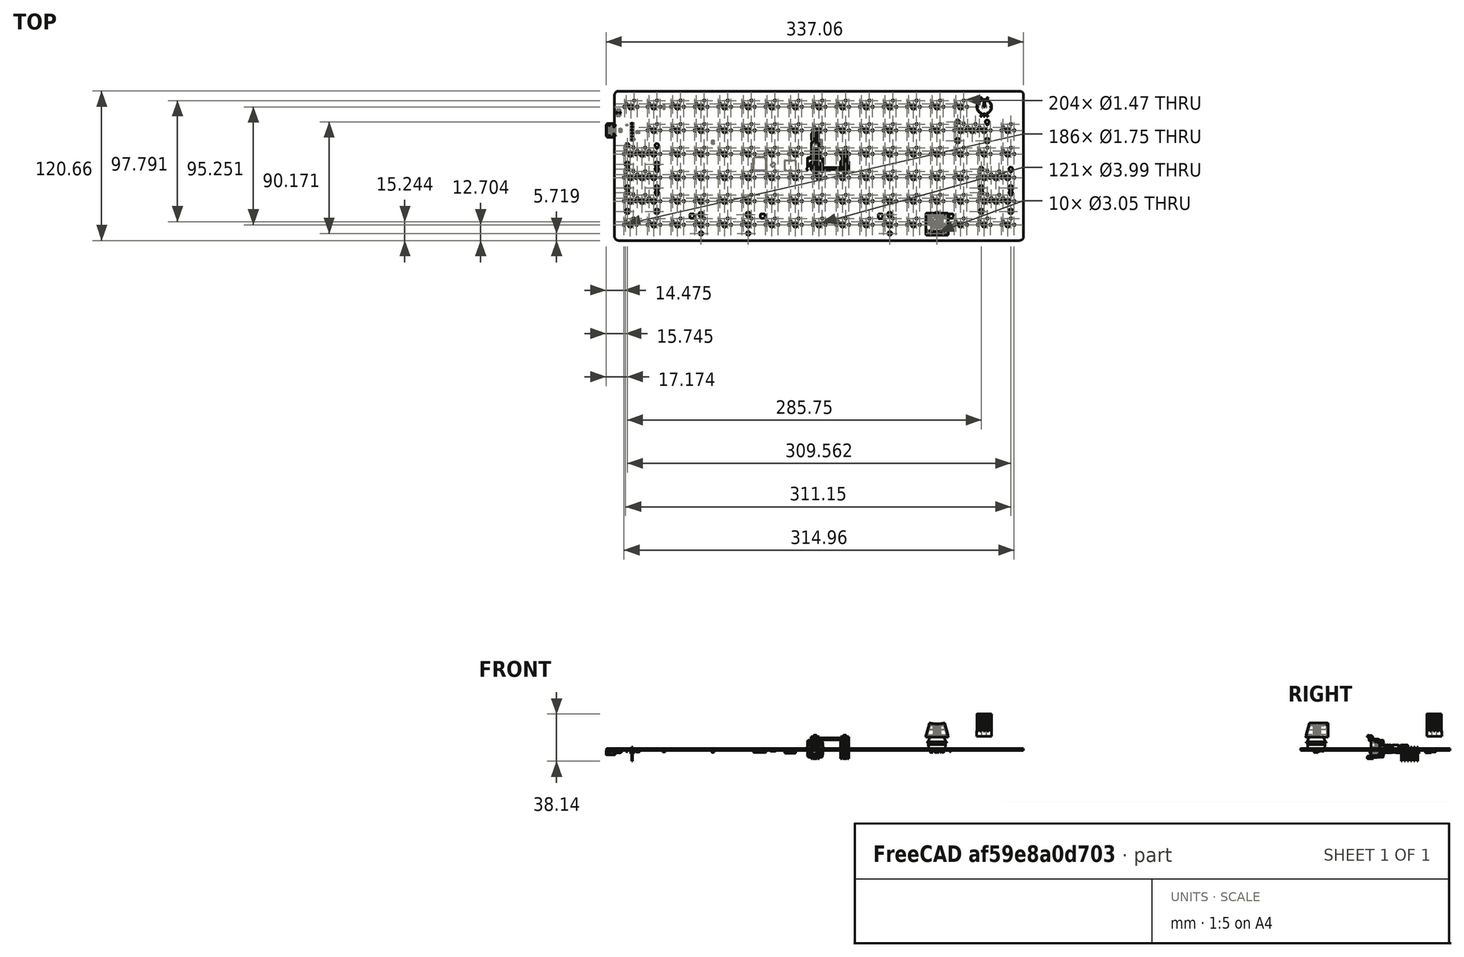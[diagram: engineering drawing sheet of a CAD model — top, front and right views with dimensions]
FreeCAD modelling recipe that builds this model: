
FCSTD DOCUMENT  (FreeCAD 0.19R24291 (Git))
Label: Orthonite87_003
License: All rights reserved
LicenseURL: http://en.wikipedia.org/wiki/All_rights_reserved
objects: App::Link×376, Part::Feature×31, App::Part×8, PartDesign::CoordinateSystem×1, Sketcher::SketchObject×1
note: 33 computed .brp shape members not serialized (recipe doc carries the construction recipe); baked Part::Feature solids carry a one-line shape summary decoded from their .brp

FEATURE [PartDesign::CoordinateSystem] Local_CS_e1db
  AttacherType = Attacher::AttachEngine3D
FEATURE [Part::Feature] Pcb_e1db
  Placement = pos=(-174.625,80.9625,0) rot=(0,0,1;0rad)
  shape: bbox 336.6 x 120.7 x 1.6 mm, 675 faces (baked)
FEATURE [Sketcher::SketchObject] PCB_Sketch_e1db
  FullyConstrained = false
  sketch-geometry (18):
    g0: LineSegment StartX=-168.275 StartY=33.3375 StartZ=0 EndX=-168.275 EndY=23.8125 EndZ=0
    g1: LineSegment StartX=-163.512 StartY=23.0188 StartZ=0 EndX=-162.719 EndY=23.0188 EndZ=0
    g2: LineSegment StartX=-163.512 StartY=34.1313 StartZ=0 EndX=-162.719 EndY=34.1313 EndZ=0
    g3: LineSegment StartX=-167.481 StartY=34.1313 StartZ=0 EndX=-163.512 EndY=34.1313 EndZ=0
    g4: LineSegment StartX=-163.512 StartY=23.0188 StartZ=0 EndX=-167.481 EndY=23.0188 EndZ=0
    g5: LineSegment StartX=-161.925 StartY=22.225 StartZ=0 EndX=-161.925 EndY=-57.15 EndZ=0
    g6: LineSegment StartX=-161.925 StartY=57.15 StartZ=0 EndX=-161.925 EndY=34.925 EndZ=0
    g7: LineSegment StartX=168.275 StartY=-57.15 StartZ=0 EndX=168.275 EndY=57.15 EndZ=0
    g8: LineSegment StartX=-158.75 StartY=-60.325 StartZ=0 EndX=165.1 EndY=-60.325 EndZ=0
    g9: LineSegment StartX=-158.75 StartY=60.325 StartZ=0 EndX=165.1 EndY=60.325 EndZ=0
    g10: ArcOfCircle CenterX=-167.481 CenterY=33.3375 CenterZ=0 NormalX=0 NormalY=0 NormalZ=1 AngleXU=0 Radius=0.79375 StartAngle=1.5708 EndAngle=3.14159
    g11: ArcOfCircle CenterX=-167.481 CenterY=23.8125 CenterZ=0 NormalX=0 NormalY=0 NormalZ=1 AngleXU=0 Radius=0.79375 StartAngle=3.14159 EndAngle=4.71239
    g12: ArcOfCircle CenterX=-162.719 CenterY=22.225 CenterZ=0 NormalX=0 NormalY=0 NormalZ=1 AngleXU=0 Radius=0.79375 StartAngle=0 EndAngle=1.5708
    g13: ArcOfCircle CenterX=-162.719 CenterY=34.925 CenterZ=0 NormalX=0 NormalY=0 NormalZ=1 AngleXU=0 Radius=0.79375 StartAngle=4.71239 EndAngle=6.28319
    g14: ArcOfCircle CenterX=165.1 CenterY=-57.15 CenterZ=0 NormalX=0 NormalY=0 NormalZ=1 AngleXU=0 Radius=3.175 StartAngle=4.71239 EndAngle=6.28319
    g15: ArcOfCircle CenterX=-158.75 CenterY=-57.15 CenterZ=0 NormalX=0 NormalY=0 NormalZ=1 AngleXU=0 Radius=3.175 StartAngle=3.14159 EndAngle=4.71239
    g16: ArcOfCircle CenterX=-158.75 CenterY=57.15 CenterZ=0 NormalX=0 NormalY=0 NormalZ=1 AngleXU=0 Radius=3.175 StartAngle=1.5708 EndAngle=3.14159
    g17: ArcOfCircle CenterX=165.1 CenterY=57.15 CenterZ=0 NormalX=0 NormalY=0 NormalZ=1 AngleXU=0 Radius=3.175 StartAngle=0 EndAngle=1.5708
FEATURE [Part::Feature] Shape  label="K_105_cherry mx_611CBFA4"
  Placement = pos=(98.425,-47.6255,5.5) rot=(0,0.707107,0.707107;3.14159rad)
  shape: bbox 15.64 x 16.33 x 17.85 mm, 92 faces (baked)
FEATURE [Part::Feature] Shape001  label="K_105_MX 轴标准键帽__¨¹_¡À__¡§1__¨¤_611CBFA4[2]"
  Placement = pos=(89.425,-38.1255,9.5) rot=(1,0,0;1.5708rad)
  shape: bbox 18.01 x 18 x 11.38 mm, 348 faces (baked)
FEATURE [App::Link] K_105_cherry_mx_611CBFA4_ln_  label="K_108_105_cherry mx_611DE0BA"
  LinkPlacement = pos=(155.575,-47.6255,5.5) rot=(0,0.707107,0.707107;3.14159rad)
  LinkedObject = -> Shape
  Placement = pos=(155.575,-47.6255,5.5) rot=(0,0.707107,0.707107;3.14159rad)
FEATURE [App::Link] K_105_MX______________________________________1_______611CBFA4_2__ln_  label="K_108_105_MX 轴标准键帽__¨¹_¡À__¡§1__¨¤_611DE0BA[2]"
  LinkPlacement = pos=(146.575,-38.1255,9.5) rot=(1,0,0;1.5708rad)
  LinkedObject = -> Shape001
  Placement = pos=(146.575,-38.1255,9.5) rot=(1,0,0;1.5708rad)
FEATURE [App::Link] K_105_cherry_mx_611CBFA4_ln_001  label="K_107_105_cherry mx_611DE0A5"
  LinkPlacement = pos=(136.525,-47.6255,5.5) rot=(0,0.707107,0.707107;3.14159rad)
  LinkedObject = -> Shape
  Placement = pos=(136.525,-47.6255,5.5) rot=(0,0.707107,0.707107;3.14159rad)
FEATURE [App::Link] K_105_MX______________________________________1_______611CBFA4_2__ln_001  label="K_107_105_MX 轴标准键帽__¨¹_¡À__¡§1__¨¤_611DE0A5[2]"
  LinkPlacement = pos=(127.525,-38.1255,9.5) rot=(1,0,0;1.5708rad)
  LinkedObject = -> Shape001
  Placement = pos=(127.525,-38.1255,9.5) rot=(1,0,0;1.5708rad)
FEATURE [App::Link] K_105_cherry_mx_611CBFA4_ln_002  label="K_106_105_cherry mx_611DE090"
  LinkPlacement = pos=(117.475,-47.6255,5.5) rot=(0,0.707107,0.707107;3.14159rad)
  LinkedObject = -> Shape
  Placement = pos=(117.475,-47.6255,5.5) rot=(0,0.707107,0.707107;3.14159rad)
FEATURE [App::Link] K_105_MX______________________________________1_______611CBFA4_2__ln_002  label="K_106_105_MX 轴标准键帽__¨¹_¡À__¡§1__¨¤_611DE090[2]"
  LinkPlacement = pos=(108.475,-38.1255,9.5) rot=(1,0,0;1.5708rad)
  LinkedObject = -> Shape001
  Placement = pos=(108.475,-38.1255,9.5) rot=(1,0,0;1.5708rad)
FEATURE [App::Link] K_105_cherry_mx_611CBFA4_ln_003  label="K_103_105_cherry mx_611DE023"
  LinkPlacement = pos=(60.325,-47.6255,5.5) rot=(0,0.707107,0.707107;3.14159rad)
  LinkedObject = -> Shape
  Placement = pos=(60.325,-47.6255,5.5) rot=(0,0.707107,0.707107;3.14159rad)
FEATURE [App::Link] K_105_MX______________________________________1_______611CBFA4_2__ln_003  label="K_103_105_MX 轴标准键帽__¨¹_¡À__¡§1__¨¤_611DE023[2]"
  LinkPlacement = pos=(51.325,-38.1255,9.5) rot=(1,0,0;1.5708rad)
  LinkedObject = -> Shape001
  Placement = pos=(51.325,-38.1255,9.5) rot=(1,0,0;1.5708rad)
FEATURE [App::Link] K_105_cherry_mx_611CBFA4_ln_004  label="K_102_105_cherry mx_611DE00E"
  LinkPlacement = pos=(41.275,-47.6255,5.5) rot=(0,0.707107,0.707107;3.14159rad)
  LinkedObject = -> Shape
  Placement = pos=(41.275,-47.6255,5.5) rot=(0,0.707107,0.707107;3.14159rad)
FEATURE [App::Link] K_105_MX______________________________________1_______611CBFA4_2__ln_004  label="K_102_105_MX 轴标准键帽__¨¹_¡À__¡§1__¨¤_611DE00E[2]"
  LinkPlacement = pos=(32.275,-38.1255,9.5) rot=(1,0,0;1.5708rad)
  LinkedObject = -> Shape001
  Placement = pos=(32.275,-38.1255,9.5) rot=(1,0,0;1.5708rad)
FEATURE [App::Link] K_105_cherry_mx_611CBFA4_ln_005  label="K_101_105_cherry mx_611DDFF9"
  LinkPlacement = pos=(22.225,-47.6255,5.5) rot=(0,0.707107,0.707107;3.14159rad)
  LinkedObject = -> Shape
  Placement = pos=(22.225,-47.6255,5.5) rot=(0,0.707107,0.707107;3.14159rad)
FEATURE [App::Link] K_105_MX______________________________________1_______611CBFA4_2__ln_005  label="K_101_105_MX 轴标准键帽__¨¹_¡À__¡§1__¨¤_611DDFF9[2]"
  LinkPlacement = pos=(13.225,-38.1255,9.5) rot=(1,0,0;1.5708rad)
  LinkedObject = -> Shape001
  Placement = pos=(13.225,-38.1255,9.5) rot=(1,0,0;1.5708rad)
FEATURE [App::Link] K_105_cherry_mx_611CBFA4_ln_006  label="K_100_105_cherry mx_611DDFE4"
  LinkPlacement = pos=(3.175,-47.6255,5.5) rot=(0,0.707107,0.707107;3.14159rad)
  LinkedObject = -> Shape
  Placement = pos=(3.175,-47.6255,5.5) rot=(0,0.707107,0.707107;3.14159rad)
FEATURE [App::Link] K_105_MX______________________________________1_______611CBFA4_2__ln_006  label="K_100_105_MX 轴标准键帽__¨¹_¡À__¡§1__¨¤_611DDFE4[2]"
  LinkPlacement = pos=(-5.825,-38.1255,9.5) rot=(1,0,0;1.5708rad)
  LinkedObject = -> Shape001
  Placement = pos=(-5.825,-38.1255,9.5) rot=(1,0,0;1.5708rad)
FEATURE [App::Link] K_105_cherry_mx_611CBFA4_ln_007  label="K_2_105_cherry mx_611DD732"
  LinkPlacement = pos=(-148.717,47.625,5.5) rot=(0,0.707107,0.707107;3.14159rad)
  LinkedObject = -> Shape
  Placement = pos=(-148.717,47.625,5.5) rot=(0,0.707107,0.707107;3.14159rad)
FEATURE [App::Link] K_105_MX______________________________________1_______611CBFA4_2__ln_007  label="K_2_105_MX 轴标准键帽__¨¹_¡À__¡§1__¨¤_611DD732[2]"
  LinkPlacement = pos=(-157.717,57.125,9.5) rot=(1,0,0;1.5708rad)
  LinkedObject = -> Shape001
  Placement = pos=(-157.717,57.125,9.5) rot=(1,0,0;1.5708rad)
FEATURE [App::Link] K_105_cherry_mx_611CBFA4_ln_008  label="K_9_105_cherry mx_611DD7C5"
  LinkPlacement = pos=(-15.875,47.625,5.5) rot=(0,0.707107,0.707107;3.14159rad)
  LinkedObject = -> Shape
  Placement = pos=(-15.875,47.625,5.5) rot=(0,0.707107,0.707107;3.14159rad)
FEATURE [App::Link] K_105_MX______________________________________1_______611CBFA4_2__ln_008  label="K_9_105_MX 轴标准键帽__¨¹_¡À__¡§1__¨¤_611DD7C5[2]"
  LinkPlacement = pos=(-24.875,57.125,9.5) rot=(1,0,0;1.5708rad)
  LinkedObject = -> Shape001
  Placement = pos=(-24.875,57.125,9.5) rot=(1,0,0;1.5708rad)
FEATURE [App::Link] K_105_cherry_mx_611CBFA4_ln_009  label="K_8_105_cherry mx_611DD7B0"
  LinkPlacement = pos=(-34.925,47.625,5.5) rot=(0,0.707107,0.707107;3.14159rad)
  LinkedObject = -> Shape
  Placement = pos=(-34.925,47.625,5.5) rot=(0,0.707107,0.707107;3.14159rad)
FEATURE [App::Link] K_105_MX______________________________________1_______611CBFA4_2__ln_009  label="K_8_105_MX 轴标准键帽__¨¹_¡À__¡§1__¨¤_611DD7B0[2]"
  LinkPlacement = pos=(-43.925,57.125,9.5) rot=(1,0,0;1.5708rad)
  LinkedObject = -> Shape001
  Placement = pos=(-43.925,57.125,9.5) rot=(1,0,0;1.5708rad)
FEATURE [App::Link] K_105_cherry_mx_611CBFA4_ln_010  label="K_7_105_cherry mx_611DD79B"
  LinkPlacement = pos=(-53.975,47.625,5.5) rot=(0,0.707107,0.707107;3.14159rad)
  LinkedObject = -> Shape
  Placement = pos=(-53.975,47.625,5.5) rot=(0,0.707107,0.707107;3.14159rad)
FEATURE [App::Link] K_105_MX______________________________________1_______611CBFA4_2__ln_010  label="K_7_105_MX 轴标准键帽__¨¹_¡À__¡§1__¨¤_611DD79B[2]"
  LinkPlacement = pos=(-62.975,57.125,9.5) rot=(1,0,0;1.5708rad)
  LinkedObject = -> Shape001
  Placement = pos=(-62.975,57.125,9.5) rot=(1,0,0;1.5708rad)
FEATURE [App::Link] K_105_cherry_mx_611CBFA4_ln_011  label="K_6_105_cherry mx_611DD786"
  LinkPlacement = pos=(-73.025,47.625,5.5) rot=(0,0.707107,0.707107;3.14159rad)
  LinkedObject = -> Shape
  Placement = pos=(-73.025,47.625,5.5) rot=(0,0.707107,0.707107;3.14159rad)
FEATURE [App::Link] K_105_MX______________________________________1_______611CBFA4_2__ln_011  label="K_6_105_MX 轴标准键帽__¨¹_¡À__¡§1__¨¤_611DD786[2]"
  LinkPlacement = pos=(-82.025,57.125,9.5) rot=(1,0,0;1.5708rad)
  LinkedObject = -> Shape001
  Placement = pos=(-82.025,57.125,9.5) rot=(1,0,0;1.5708rad)
FEATURE [App::Link] K_105_cherry_mx_611CBFA4_ln_012  label="K_5_105_cherry mx_611DD771"
  LinkPlacement = pos=(-92.075,47.625,5.5) rot=(0,0.707107,0.707107;3.14159rad)
  LinkedObject = -> Shape
  Placement = pos=(-92.075,47.625,5.5) rot=(0,0.707107,0.707107;3.14159rad)
FEATURE [App::Link] K_105_MX______________________________________1_______611CBFA4_2__ln_012  label="K_5_105_MX 轴标准键帽__¨¹_¡À__¡§1__¨¤_611DD771[2]"
  LinkPlacement = pos=(-101.075,57.125,9.5) rot=(1,0,0;1.5708rad)
  LinkedObject = -> Shape001
  Placement = pos=(-101.075,57.125,9.5) rot=(1,0,0;1.5708rad)
FEATURE [App::Link] K_105_cherry_mx_611CBFA4_ln_013  label="K_4_105_cherry mx_611DD75C"
  LinkPlacement = pos=(-111.125,47.625,5.5) rot=(0,0.707107,0.707107;3.14159rad)
  LinkedObject = -> Shape
  Placement = pos=(-111.125,47.625,5.5) rot=(0,0.707107,0.707107;3.14159rad)
FEATURE [App::Link] K_105_MX______________________________________1_______611CBFA4_2__ln_013  label="K_4_105_MX 轴标准键帽__¨¹_¡À__¡§1__¨¤_611DD75C[2]"
  LinkPlacement = pos=(-120.125,57.125,9.5) rot=(1,0,0;1.5708rad)
  LinkedObject = -> Shape001
  Placement = pos=(-120.125,57.125,9.5) rot=(1,0,0;1.5708rad)
FEATURE [App::Link] K_105_cherry_mx_611CBFA4_ln_014  label="K_3_105_cherry mx_611DD747"
  LinkPlacement = pos=(-130.175,47.625,5.5) rot=(0,0.707107,0.707107;3.14159rad)
  LinkedObject = -> Shape
  Placement = pos=(-130.175,47.625,5.5) rot=(0,0.707107,0.707107;3.14159rad)
FEATURE [App::Link] K_105_MX______________________________________1_______611CBFA4_2__ln_014  label="K_3_105_MX 轴标准键帽__¨¹_¡À__¡§1__¨¤_611DD747[2]"
  LinkPlacement = pos=(-139.175,57.125,9.5) rot=(1,0,0;1.5708rad)
  LinkedObject = -> Shape001
  Placement = pos=(-139.175,57.125,9.5) rot=(1,0,0;1.5708rad)
FEATURE [App::Link] K_105_cherry_mx_611CBFA4_ln_015  label="K_33_105_cherry mx_611E8F84"
  LinkPlacement = pos=(155.575,28.575,5.5) rot=(0,0.707107,0.707107;3.14159rad)
  LinkedObject = -> Shape
  Placement = pos=(155.575,28.575,5.5) rot=(0,0.707107,0.707107;3.14159rad)
FEATURE [App::Link] K_105_MX______________________________________1_______611CBFA4_2__ln_015  label="K_33_105_MX 轴标准键帽__¨¹_¡À__¡§1__¨¤_611E8F84[2]"
  LinkPlacement = pos=(146.575,38.075,9.5) rot=(1,0,0;1.5708rad)
  LinkedObject = -> Shape001
  Placement = pos=(146.575,38.075,9.5) rot=(1,0,0;1.5708rad)
FEATURE [App::Link] K_105_cherry_mx_611CBFA4_ln_016  label="K_99_105_cherry mx_611DDFCF"
  LinkPlacement = pos=(-15.875,-47.6255,5.5) rot=(0,0.707107,0.707107;3.14159rad)
  LinkedObject = -> Shape
  Placement = pos=(-15.875,-47.6255,5.5) rot=(0,0.707107,0.707107;3.14159rad)
FEATURE [App::Link] K_105_MX______________________________________1_______611CBFA4_2__ln_016  label="K_99_105_MX 轴标准键帽__¨¹_¡À__¡§1__¨¤_611DDFCF[2]"
  LinkPlacement = pos=(-24.875,-38.1255,9.5) rot=(1,0,0;1.5708rad)
  LinkedObject = -> Shape001
  Placement = pos=(-24.875,-38.1255,9.5) rot=(1,0,0;1.5708rad)
FEATURE [App::Link] K_105_cherry_mx_611CBFA4_ln_017  label="K_98_105_cherry mx_611DDFBA"
  LinkPlacement = pos=(-34.925,-47.6255,5.5) rot=(0,0.707107,0.707107;3.14159rad)
  LinkedObject = -> Shape
  Placement = pos=(-34.925,-47.6255,5.5) rot=(0,0.707107,0.707107;3.14159rad)
FEATURE [App::Link] K_105_MX______________________________________1_______611CBFA4_2__ln_017  label="K_98_105_MX 轴标准键帽__¨¹_¡À__¡§1__¨¤_611DDFBA[2]"
  LinkPlacement = pos=(-43.925,-38.1255,9.5) rot=(1,0,0;1.5708rad)
  LinkedObject = -> Shape001
  Placement = pos=(-43.925,-38.1255,9.5) rot=(1,0,0;1.5708rad)
FEATURE [App::Link] K_105_cherry_mx_611CBFA4_ln_018  label="K_97_105_cherry mx_611DDFA5"
  LinkPlacement = pos=(-53.975,-47.6255,5.5) rot=(0,0.707107,0.707107;3.14159rad)
  LinkedObject = -> Shape
  Placement = pos=(-53.975,-47.6255,5.5) rot=(0,0.707107,0.707107;3.14159rad)
FEATURE [App::Link] K_105_MX______________________________________1_______611CBFA4_2__ln_018  label="K_97_105_MX 轴标准键帽__¨¹_¡À__¡§1__¨¤_611DDFA5[2]"
  LinkPlacement = pos=(-62.975,-38.1255,9.5) rot=(1,0,0;1.5708rad)
  LinkedObject = -> Shape001
  Placement = pos=(-62.975,-38.1255,9.5) rot=(1,0,0;1.5708rad)
FEATURE [App::Link] K_105_cherry_mx_611CBFA4_ln_019  label="K_95_105_cherry mx_611DDF60"
  LinkPlacement = pos=(-92.075,-47.6255,5.5) rot=(0,0.707107,0.707107;3.14159rad)
  LinkedObject = -> Shape
  Placement = pos=(-92.075,-47.6255,5.5) rot=(0,0.707107,0.707107;3.14159rad)
FEATURE [App::Link] K_105_MX______________________________________1_______611CBFA4_2__ln_019  label="K_95_105_MX 轴标准键帽__¨¹_¡À__¡§1__¨¤_611DDF60[2]"
  LinkPlacement = pos=(-101.075,-38.1255,9.5) rot=(1,0,0;1.5708rad)
  LinkedObject = -> Shape001
  Placement = pos=(-101.075,-38.1255,9.5) rot=(1,0,0;1.5708rad)
FEATURE [App::Link] K_105_cherry_mx_611CBFA4_ln_020  label="K_94_105_cherry mx_611DDF4B"
  LinkPlacement = pos=(-111.125,-47.6255,5.5) rot=(0,0.707107,0.707107;3.14159rad)
  LinkedObject = -> Shape
  Placement = pos=(-111.125,-47.6255,5.5) rot=(0,0.707107,0.707107;3.14159rad)
FEATURE [App::Link] K_105_MX______________________________________1_______611CBFA4_2__ln_020  label="K_94_105_MX 轴标准键帽__¨¹_¡À__¡§1__¨¤_611DDF4B[2]"
  LinkPlacement = pos=(-120.125,-38.1255,9.5) rot=(1,0,0;1.5708rad)
  LinkedObject = -> Shape001
  Placement = pos=(-120.125,-38.1255,9.5) rot=(1,0,0;1.5708rad)
FEATURE [App::Link] K_105_cherry_mx_611CBFA4_ln_021  label="K_93_105_cherry mx_611DDF36"
  LinkPlacement = pos=(-130.175,-47.6255,5.5) rot=(0,0.707107,0.707107;3.14159rad)
  LinkedObject = -> Shape
  Placement = pos=(-130.175,-47.6255,5.5) rot=(0,0.707107,0.707107;3.14159rad)
FEATURE [App::Link] K_105_MX______________________________________1_______611CBFA4_2__ln_021  label="K_93_105_MX 轴标准键帽__¨¹_¡À__¡§1__¨¤_611DDF36[2]"
  LinkPlacement = pos=(-139.175,-38.1255,9.5) rot=(1,0,0;1.5708rad)
  LinkedObject = -> Shape001
  Placement = pos=(-139.175,-38.1255,9.5) rot=(1,0,0;1.5708rad)
FEATURE [App::Link] K_105_cherry_mx_611CBFA4_ln_022  label="K_92_105_cherry mx_611DDF21"
  LinkPlacement = pos=(-149.225,-47.6255,5.5) rot=(0,0.707107,0.707107;3.14159rad)
  LinkedObject = -> Shape
  Placement = pos=(-149.225,-47.6255,5.5) rot=(0,0.707107,0.707107;3.14159rad)
FEATURE [App::Link] K_105_MX______________________________________1_______611CBFA4_2__ln_022  label="K_92_105_MX 轴标准键帽__¨¹_¡À__¡§1__¨¤_611DDF21[2]"
  LinkPlacement = pos=(-158.225,-38.1255,9.5) rot=(1,0,0;1.5708rad)
  LinkedObject = -> Shape001
  Placement = pos=(-158.225,-38.1255,9.5) rot=(1,0,0;1.5708rad)
FEATURE [App::Link] K_105_cherry_mx_611CBFA4_ln_023  label="K_88_105_cherry mx_611DDEB2"
  LinkPlacement = pos=(136.525,-28.5755,5.5) rot=(0,0.707107,0.707107;3.14159rad)
  LinkedObject = -> Shape
  Placement = pos=(136.525,-28.5755,5.5) rot=(0,0.707107,0.707107;3.14159rad)
FEATURE [App::Link] K_105_MX______________________________________1_______611CBFA4_2__ln_023  label="K_88_105_MX 轴标准键帽__¨¹_¡À__¡§1__¨¤_611DDEB2[2]"
  LinkPlacement = pos=(127.525,-19.0755,9.5) rot=(1,0,0;1.5708rad)
  LinkedObject = -> Shape001
  Placement = pos=(127.525,-19.0755,9.5) rot=(1,0,0;1.5708rad)
FEATURE [App::Link] K_105_cherry_mx_611CBFA4_ln_024  label="K_87_105_cherry mx_611DDE9D"
  LinkPlacement = pos=(117.475,-28.5755,5.5) rot=(0,0.707107,0.707107;3.14159rad)
  LinkedObject = -> Shape
  Placement = pos=(117.475,-28.5755,5.5) rot=(0,0.707107,0.707107;3.14159rad)
FEATURE [App::Link] K_105_MX______________________________________1_______611CBFA4_2__ln_024  label="K_87_105_MX 轴标准键帽__¨¹_¡À__¡§1__¨¤_611DDE9D[2]"
  LinkPlacement = pos=(108.475,-19.0755,9.5) rot=(1,0,0;1.5708rad)
  LinkedObject = -> Shape001
  Placement = pos=(108.475,-19.0755,9.5) rot=(1,0,0;1.5708rad)
FEATURE [App::Link] K_105_cherry_mx_611CBFA4_ln_025  label="K_86_105_cherry mx_611DDE88"
  LinkPlacement = pos=(98.425,-28.5755,5.5) rot=(0,0.707107,0.707107;3.14159rad)
  LinkedObject = -> Shape
  Placement = pos=(98.425,-28.5755,5.5) rot=(0,0.707107,0.707107;3.14159rad)
FEATURE [App::Link] K_105_MX______________________________________1_______611CBFA4_2__ln_025  label="K_86_105_MX 轴标准键帽__¨¹_¡À__¡§1__¨¤_611DDE88[2]"
  LinkPlacement = pos=(89.425,-19.0755,9.5) rot=(1,0,0;1.5708rad)
  LinkedObject = -> Shape001
  Placement = pos=(89.425,-19.0755,9.5) rot=(1,0,0;1.5708rad)
FEATURE [App::Link] K_105_cherry_mx_611CBFA4_ln_026  label="K_85_105_cherry mx_611DDE73"
  LinkPlacement = pos=(79.375,-28.5755,5.5) rot=(0,0.707107,0.707107;3.14159rad)
  LinkedObject = -> Shape
  Placement = pos=(79.375,-28.5755,5.5) rot=(0,0.707107,0.707107;3.14159rad)
FEATURE [App::Link] K_105_MX______________________________________1_______611CBFA4_2__ln_026  label="K_85_105_MX 轴标准键帽__¨¹_¡À__¡§1__¨¤_611DDE73[2]"
  LinkPlacement = pos=(70.375,-19.0755,9.5) rot=(1,0,0;1.5708rad)
  LinkedObject = -> Shape001
  Placement = pos=(70.375,-19.0755,9.5) rot=(1,0,0;1.5708rad)
FEATURE [App::Link] K_105_cherry_mx_611CBFA4_ln_027  label="K_84_105_cherry mx_611DDE5E"
  LinkPlacement = pos=(60.325,-28.5755,5.5) rot=(0,0.707107,0.707107;3.14159rad)
  LinkedObject = -> Shape
  Placement = pos=(60.325,-28.5755,5.5) rot=(0,0.707107,0.707107;3.14159rad)
FEATURE [App::Link] K_105_MX______________________________________1_______611CBFA4_2__ln_027  label="K_84_105_MX 轴标准键帽__¨¹_¡À__¡§1__¨¤_611DDE5E[2]"
  LinkPlacement = pos=(51.325,-19.0755,9.5) rot=(1,0,0;1.5708rad)
  LinkedObject = -> Shape001
  Placement = pos=(51.325,-19.0755,9.5) rot=(1,0,0;1.5708rad)
FEATURE [App::Link] K_105_cherry_mx_611CBFA4_ln_028  label="K_83_105_cherry mx_611DDE49"
  LinkPlacement = pos=(41.275,-28.5755,5.5) rot=(0,0.707107,0.707107;3.14159rad)
  LinkedObject = -> Shape
  Placement = pos=(41.275,-28.5755,5.5) rot=(0,0.707107,0.707107;3.14159rad)
FEATURE [App::Link] K_105_MX______________________________________1_______611CBFA4_2__ln_028  label="K_83_105_MX 轴标准键帽__¨¹_¡À__¡§1__¨¤_611DDE49[2]"
  LinkPlacement = pos=(32.275,-19.0755,9.5) rot=(1,0,0;1.5708rad)
  LinkedObject = -> Shape001
  Placement = pos=(32.275,-19.0755,9.5) rot=(1,0,0;1.5708rad)
FEATURE [App::Link] K_105_cherry_mx_611CBFA4_ln_029  label="K_82_105_cherry mx_611DDE34"
  LinkPlacement = pos=(22.225,-28.5755,5.5) rot=(0,0.707107,0.707107;3.14159rad)
  LinkedObject = -> Shape
  Placement = pos=(22.225,-28.5755,5.5) rot=(0,0.707107,0.707107;3.14159rad)
FEATURE [App::Link] K_105_MX______________________________________1_______611CBFA4_2__ln_029  label="K_82_105_MX 轴标准键帽__¨¹_¡À__¡§1__¨¤_611DDE34[2]"
  LinkPlacement = pos=(13.225,-19.0755,9.5) rot=(1,0,0;1.5708rad)
  LinkedObject = -> Shape001
  Placement = pos=(13.225,-19.0755,9.5) rot=(1,0,0;1.5708rad)
FEATURE [App::Link] K_105_cherry_mx_611CBFA4_ln_030  label="K_81_105_cherry mx_611DDE1F"
  LinkPlacement = pos=(3.175,-28.5755,5.5) rot=(0,0.707107,0.707107;3.14159rad)
  LinkedObject = -> Shape
  Placement = pos=(3.175,-28.5755,5.5) rot=(0,0.707107,0.707107;3.14159rad)
FEATURE [App::Link] K_105_MX______________________________________1_______611CBFA4_2__ln_030  label="K_81_105_MX 轴标准键帽__¨¹_¡À__¡§1__¨¤_611DDE1F[2]"
  LinkPlacement = pos=(-5.825,-19.0755,9.5) rot=(1,0,0;1.5708rad)
  LinkedObject = -> Shape001
  Placement = pos=(-5.825,-19.0755,9.5) rot=(1,0,0;1.5708rad)
FEATURE [App::Link] K_105_cherry_mx_611CBFA4_ln_031  label="K_80_105_cherry mx_611DDE0A"
  LinkPlacement = pos=(-15.875,-28.5755,5.5) rot=(0,0.707107,0.707107;3.14159rad)
  LinkedObject = -> Shape
  Placement = pos=(-15.875,-28.5755,5.5) rot=(0,0.707107,0.707107;3.14159rad)
FEATURE [App::Link] K_105_MX______________________________________1_______611CBFA4_2__ln_031  label="K_80_105_MX 轴标准键帽__¨¹_¡À__¡§1__¨¤_611DDE0A[2]"
  LinkPlacement = pos=(-24.875,-19.0755,9.5) rot=(1,0,0;1.5708rad)
  LinkedObject = -> Shape001
  Placement = pos=(-24.875,-19.0755,9.5) rot=(1,0,0;1.5708rad)
FEATURE [App::Link] K_105_cherry_mx_611CBFA4_ln_032  label="K_79_105_cherry mx_611DDDF5"
  LinkPlacement = pos=(-34.925,-28.5755,5.5) rot=(0,0.707107,0.707107;3.14159rad)
  LinkedObject = -> Shape
  Placement = pos=(-34.925,-28.5755,5.5) rot=(0,0.707107,0.707107;3.14159rad)
FEATURE [App::Link] K_105_MX______________________________________1_______611CBFA4_2__ln_032  label="K_79_105_MX 轴标准键帽__¨¹_¡À__¡§1__¨¤_611DDDF5[2]"
  LinkPlacement = pos=(-43.925,-19.0755,9.5) rot=(1,0,0;1.5708rad)
  LinkedObject = -> Shape001
  Placement = pos=(-43.925,-19.0755,9.5) rot=(1,0,0;1.5708rad)
FEATURE [App::Link] K_105_cherry_mx_611CBFA4_ln_033  label="K_78_105_cherry mx_611DDDE0"
  LinkPlacement = pos=(-53.975,-28.5755,5.5) rot=(0,0.707107,0.707107;3.14159rad)
  LinkedObject = -> Shape
  Placement = pos=(-53.975,-28.5755,5.5) rot=(0,0.707107,0.707107;3.14159rad)
FEATURE [App::Link] K_105_MX______________________________________1_______611CBFA4_2__ln_033  label="K_78_105_MX 轴标准键帽__¨¹_¡À__¡§1__¨¤_611DDDE0[2]"
  LinkPlacement = pos=(-62.975,-19.0755,9.5) rot=(1,0,0;1.5708rad)
  LinkedObject = -> Shape001
  Placement = pos=(-62.975,-19.0755,9.5) rot=(1,0,0;1.5708rad)
FEATURE [App::Link] K_105_cherry_mx_611CBFA4_ln_034  label="K_77_105_cherry mx_611DDDCB"
  LinkPlacement = pos=(-73.025,-28.5755,5.5) rot=(0,0.707107,0.707107;3.14159rad)
  LinkedObject = -> Shape
  Placement = pos=(-73.025,-28.5755,5.5) rot=(0,0.707107,0.707107;3.14159rad)
FEATURE [App::Link] K_105_MX______________________________________1_______611CBFA4_2__ln_034  label="K_77_105_MX 轴标准键帽__¨¹_¡À__¡§1__¨¤_611DDDCB[2]"
  LinkPlacement = pos=(-82.025,-19.0755,9.5) rot=(1,0,0;1.5708rad)
  LinkedObject = -> Shape001
  Placement = pos=(-82.025,-19.0755,9.5) rot=(1,0,0;1.5708rad)
FEATURE [App::Link] K_105_cherry_mx_611CBFA4_ln_035  label="K_76_105_cherry mx_611DDDB6"
  LinkPlacement = pos=(-92.075,-28.5755,5.5) rot=(0,0.707107,0.707107;3.14159rad)
  LinkedObject = -> Shape
  Placement = pos=(-92.075,-28.5755,5.5) rot=(0,0.707107,0.707107;3.14159rad)
FEATURE [App::Link] K_105_MX______________________________________1_______611CBFA4_2__ln_035  label="K_76_105_MX 轴标准键帽__¨¹_¡À__¡§1__¨¤_611DDDB6[2]"
  LinkPlacement = pos=(-101.075,-19.0755,9.5) rot=(1,0,0;1.5708rad)
  LinkedObject = -> Shape001
  Placement = pos=(-101.075,-19.0755,9.5) rot=(1,0,0;1.5708rad)
FEATURE [App::Link] K_105_cherry_mx_611CBFA4_ln_036  label="K_75_105_cherry mx_611DDDA1"
  LinkPlacement = pos=(-111.125,-28.5755,5.5) rot=(0,0.707107,0.707107;3.14159rad)
  LinkedObject = -> Shape
  Placement = pos=(-111.125,-28.5755,5.5) rot=(0,0.707107,0.707107;3.14159rad)
FEATURE [App::Link] K_105_MX______________________________________1_______611CBFA4_2__ln_036  label="K_75_105_MX 轴标准键帽__¨¹_¡À__¡§1__¨¤_611DDDA1[2]"
  LinkPlacement = pos=(-120.125,-19.0755,9.5) rot=(1,0,0;1.5708rad)
  LinkedObject = -> Shape001
  Placement = pos=(-120.125,-19.0755,9.5) rot=(1,0,0;1.5708rad)
FEATURE [App::Link] K_105_cherry_mx_611CBFA4_ln_037  label="K_73_105_cherry mx_611DDD5C"
  LinkPlacement = pos=(-149.225,-28.5755,5.5) rot=(0,0.707107,0.707107;3.14159rad)
  LinkedObject = -> Shape
  Placement = pos=(-149.225,-28.5755,5.5) rot=(0,0.707107,0.707107;3.14159rad)
FEATURE [App::Link] K_105_MX______________________________________1_______611CBFA4_2__ln_037  label="K_73_105_MX 轴标准键帽__¨¹_¡À__¡§1__¨¤_611DDD5C[2]"
  LinkPlacement = pos=(-158.225,-19.0755,9.5) rot=(1,0,0;1.5708rad)
  LinkedObject = -> Shape001
  Placement = pos=(-158.225,-19.0755,9.5) rot=(1,0,0;1.5708rad)
FEATURE [App::Link] K_105_cherry_mx_611CBFA4_ln_038  label="K_72_105_cherry mx_611DDD47"
  LinkPlacement = pos=(155.575,-28.5755,5.5) rot=(0,0.707107,0.707107;3.14159rad)
  LinkedObject = -> Shape
  Placement = pos=(155.575,-28.5755,5.5) rot=(0,0.707107,0.707107;3.14159rad)
FEATURE [App::Link] K_105_MX______________________________________1_______611CBFA4_2__ln_038  label="K_72_105_MX 轴标准键帽__¨¹_¡À__¡§1__¨¤_611DDD47[2]"
  LinkPlacement = pos=(146.575,-19.0755,9.5) rot=(1,0,0;1.5708rad)
  LinkedObject = -> Shape001
  Placement = pos=(146.575,-19.0755,9.5) rot=(1,0,0;1.5708rad)
FEATURE [App::Link] K_105_cherry_mx_611CBFA4_ln_039  label="K_71_105_cherry mx_611DDD32"
  LinkPlacement = pos=(-130.175,-28.5755,5.5) rot=(0,0.707107,0.707107;3.14159rad)
  LinkedObject = -> Shape
  Placement = pos=(-130.175,-28.5755,5.5) rot=(0,0.707107,0.707107;3.14159rad)
FEATURE [App::Link] K_105_MX______________________________________1_______611CBFA4_2__ln_039  label="K_71_105_MX 轴标准键帽__¨¹_¡À__¡§1__¨¤_611DDD32[2]"
  LinkPlacement = pos=(-139.175,-19.0755,9.5) rot=(1,0,0;1.5708rad)
  LinkedObject = -> Shape001
  Placement = pos=(-139.175,-19.0755,9.5) rot=(1,0,0;1.5708rad)
FEATURE [App::Link] K_105_cherry_mx_611CBFA4_ln_040  label="K_69_105_cherry mx_611DDCED"
  LinkPlacement = pos=(136.525,-9.525,5.5) rot=(0,0.707107,0.707107;3.14159rad)
  LinkedObject = -> Shape
  Placement = pos=(136.525,-9.525,5.5) rot=(0,0.707107,0.707107;3.14159rad)
FEATURE [App::Link] K_105_MX______________________________________1_______611CBFA4_2__ln_040  label="K_69_105_MX 轴标准键帽__¨¹_¡À__¡§1__¨¤_611DDCED[2]"
  LinkPlacement = pos=(127.525,-0.025,9.5) rot=(1,0,0;1.5708rad)
  LinkedObject = -> Shape001
  Placement = pos=(127.525,-0.025,9.5) rot=(1,0,0;1.5708rad)
FEATURE [App::Link] K_105_cherry_mx_611CBFA4_ln_041  label="K_68_105_cherry mx_611DDCD8"
  LinkPlacement = pos=(117.475,-9.525,5.5) rot=(0,0.707107,0.707107;3.14159rad)
  LinkedObject = -> Shape
  Placement = pos=(117.475,-9.525,5.5) rot=(0,0.707107,0.707107;3.14159rad)
FEATURE [App::Link] K_105_MX______________________________________1_______611CBFA4_2__ln_041  label="K_68_105_MX 轴标准键帽__¨¹_¡À__¡§1__¨¤_611DDCD8[2]"
  LinkPlacement = pos=(108.475,-0.025,9.5) rot=(1,0,0;1.5708rad)
  LinkedObject = -> Shape001
  Placement = pos=(108.475,-0.025,9.5) rot=(1,0,0;1.5708rad)
FEATURE [App::Link] K_105_cherry_mx_611CBFA4_ln_042  label="K_67_105_cherry mx_611DDCC3"
  LinkPlacement = pos=(98.425,-9.525,5.5) rot=(0,0.707107,0.707107;3.14159rad)
  LinkedObject = -> Shape
  Placement = pos=(98.425,-9.525,5.5) rot=(0,0.707107,0.707107;3.14159rad)
FEATURE [App::Link] K_105_MX______________________________________1_______611CBFA4_2__ln_042  label="K_67_105_MX 轴标准键帽__¨¹_¡À__¡§1__¨¤_611DDCC3[2]"
  LinkPlacement = pos=(89.425,-0.025,9.5) rot=(1,0,0;1.5708rad)
  LinkedObject = -> Shape001
  Placement = pos=(89.425,-0.025,9.5) rot=(1,0,0;1.5708rad)
FEATURE [App::Link] K_105_cherry_mx_611CBFA4_ln_043  label="K_66_105_cherry mx_611DDCAE"
  LinkPlacement = pos=(79.375,-9.525,5.5) rot=(0,0.707107,0.707107;3.14159rad)
  LinkedObject = -> Shape
  Placement = pos=(79.375,-9.525,5.5) rot=(0,0.707107,0.707107;3.14159rad)
FEATURE [App::Link] K_105_MX______________________________________1_______611CBFA4_2__ln_043  label="K_66_105_MX 轴标准键帽__¨¹_¡À__¡§1__¨¤_611DDCAE[2]"
  LinkPlacement = pos=(70.375,-0.025,9.5) rot=(1,0,0;1.5708rad)
  LinkedObject = -> Shape001
  Placement = pos=(70.375,-0.025,9.5) rot=(1,0,0;1.5708rad)
FEATURE [App::Link] K_105_cherry_mx_611CBFA4_ln_044  label="K_65_105_cherry mx_611DDC99"
  LinkPlacement = pos=(60.325,-9.525,5.5) rot=(0,0.707107,0.707107;3.14159rad)
  LinkedObject = -> Shape
  Placement = pos=(60.325,-9.525,5.5) rot=(0,0.707107,0.707107;3.14159rad)
FEATURE [App::Link] K_105_MX______________________________________1_______611CBFA4_2__ln_044  label="K_65_105_MX 轴标准键帽__¨¹_¡À__¡§1__¨¤_611DDC99[2]"
  LinkPlacement = pos=(51.325,-0.025,9.5) rot=(1,0,0;1.5708rad)
  LinkedObject = -> Shape001
  Placement = pos=(51.325,-0.025,9.5) rot=(1,0,0;1.5708rad)
FEATURE [App::Link] K_105_cherry_mx_611CBFA4_ln_045  label="K_64_105_cherry mx_611DDC84"
  LinkPlacement = pos=(41.275,-9.525,5.5) rot=(0,0.707107,0.707107;3.14159rad)
  LinkedObject = -> Shape
  Placement = pos=(41.275,-9.525,5.5) rot=(0,0.707107,0.707107;3.14159rad)
FEATURE [App::Link] K_105_MX______________________________________1_______611CBFA4_2__ln_045  label="K_64_105_MX 轴标准键帽__¨¹_¡À__¡§1__¨¤_611DDC84[2]"
  LinkPlacement = pos=(32.275,-0.025,9.5) rot=(1,0,0;1.5708rad)
  LinkedObject = -> Shape001
  Placement = pos=(32.275,-0.025,9.5) rot=(1,0,0;1.5708rad)
FEATURE [App::Link] K_105_cherry_mx_611CBFA4_ln_046  label="K_63_105_cherry mx_611DDC6F"
  LinkPlacement = pos=(22.225,-9.525,5.5) rot=(0,0.707107,0.707107;3.14159rad)
  LinkedObject = -> Shape
  Placement = pos=(22.225,-9.525,5.5) rot=(0,0.707107,0.707107;3.14159rad)
FEATURE [App::Link] K_105_MX______________________________________1_______611CBFA4_2__ln_046  label="K_63_105_MX 轴标准键帽__¨¹_¡À__¡§1__¨¤_611DDC6F[2]"
  LinkPlacement = pos=(13.225,-0.025,9.5) rot=(1,0,0;1.5708rad)
  LinkedObject = -> Shape001
  Placement = pos=(13.225,-0.025,9.5) rot=(1,0,0;1.5708rad)
FEATURE [App::Link] K_105_cherry_mx_611CBFA4_ln_047  label="K_62_105_cherry mx_611DDC5A"
  LinkPlacement = pos=(3.175,-9.525,5.5) rot=(0,0.707107,0.707107;3.14159rad)
  LinkedObject = -> Shape
  Placement = pos=(3.175,-9.525,5.5) rot=(0,0.707107,0.707107;3.14159rad)
FEATURE [App::Link] K_105_MX______________________________________1_______611CBFA4_2__ln_047  label="K_62_105_MX 轴标准键帽__¨¹_¡À__¡§1__¨¤_611DDC5A[2]"
  LinkPlacement = pos=(-5.825,-0.025,9.5) rot=(1,0,0;1.5708rad)
  LinkedObject = -> Shape001
  Placement = pos=(-5.825,-0.025,9.5) rot=(1,0,0;1.5708rad)
FEATURE [App::Link] K_105_cherry_mx_611CBFA4_ln_048  label="K_61_105_cherry mx_611DDC45"
  LinkPlacement = pos=(-15.875,-9.525,5.5) rot=(0,0.707107,0.707107;3.14159rad)
  LinkedObject = -> Shape
  Placement = pos=(-15.875,-9.525,5.5) rot=(0,0.707107,0.707107;3.14159rad)
FEATURE [App::Link] K_105_MX______________________________________1_______611CBFA4_2__ln_048  label="K_61_105_MX 轴标准键帽__¨¹_¡À__¡§1__¨¤_611DDC45[2]"
  LinkPlacement = pos=(-24.875,-0.025,9.5) rot=(1,0,0;1.5708rad)
  LinkedObject = -> Shape001
  Placement = pos=(-24.875,-0.025,9.5) rot=(1,0,0;1.5708rad)
FEATURE [App::Link] K_105_cherry_mx_611CBFA4_ln_049  label="K_60_105_cherry mx_611DDC30"
  LinkPlacement = pos=(-34.925,-9.525,5.5) rot=(0,0.707107,0.707107;3.14159rad)
  LinkedObject = -> Shape
  Placement = pos=(-34.925,-9.525,5.5) rot=(0,0.707107,0.707107;3.14159rad)
FEATURE [App::Link] K_105_MX______________________________________1_______611CBFA4_2__ln_049  label="K_60_105_MX 轴标准键帽__¨¹_¡À__¡§1__¨¤_611DDC30[2]"
  LinkPlacement = pos=(-43.925,-0.025,9.5) rot=(1,0,0;1.5708rad)
  LinkedObject = -> Shape001
  Placement = pos=(-43.925,-0.025,9.5) rot=(1,0,0;1.5708rad)
FEATURE [App::Link] K_105_cherry_mx_611CBFA4_ln_050  label="K_59_105_cherry mx_611DDC1B"
  LinkPlacement = pos=(-53.975,-9.525,5.5) rot=(0,0.707107,0.707107;3.14159rad)
  LinkedObject = -> Shape
  Placement = pos=(-53.975,-9.525,5.5) rot=(0,0.707107,0.707107;3.14159rad)
FEATURE [App::Link] K_105_MX______________________________________1_______611CBFA4_2__ln_050  label="K_59_105_MX 轴标准键帽__¨¹_¡À__¡§1__¨¤_611DDC1B[2]"
  LinkPlacement = pos=(-62.975,-0.025,9.5) rot=(1,0,0;1.5708rad)
  LinkedObject = -> Shape001
  Placement = pos=(-62.975,-0.025,9.5) rot=(1,0,0;1.5708rad)
FEATURE [App::Link] K_105_cherry_mx_611CBFA4_ln_051  label="K_58_105_cherry mx_611DDC06"
  LinkPlacement = pos=(-73.025,-9.525,5.5) rot=(0,0.707107,0.707107;3.14159rad)
  LinkedObject = -> Shape
  Placement = pos=(-73.025,-9.525,5.5) rot=(0,0.707107,0.707107;3.14159rad)
FEATURE [App::Link] K_105_MX______________________________________1_______611CBFA4_2__ln_051  label="K_58_105_MX 轴标准键帽__¨¹_¡À__¡§1__¨¤_611DDC06[2]"
  LinkPlacement = pos=(-82.025,-0.025,9.5) rot=(1,0,0;1.5708rad)
  LinkedObject = -> Shape001
  Placement = pos=(-82.025,-0.025,9.5) rot=(1,0,0;1.5708rad)
FEATURE [App::Link] K_105_cherry_mx_611CBFA4_ln_052  label="K_57_105_cherry mx_611DDBF1"
  LinkPlacement = pos=(-92.075,-9.525,5.5) rot=(0,0.707107,0.707107;3.14159rad)
  LinkedObject = -> Shape
  Placement = pos=(-92.075,-9.525,5.5) rot=(0,0.707107,0.707107;3.14159rad)
FEATURE [App::Link] K_105_MX______________________________________1_______611CBFA4_2__ln_052  label="K_57_105_MX 轴标准键帽__¨¹_¡À__¡§1__¨¤_611DDBF1[2]"
  LinkPlacement = pos=(-101.075,-0.025,9.5) rot=(1,0,0;1.5708rad)
  LinkedObject = -> Shape001
  Placement = pos=(-101.075,-0.025,9.5) rot=(1,0,0;1.5708rad)
FEATURE [App::Link] K_105_cherry_mx_611CBFA4_ln_053  label="K_56_105_cherry mx_611DDBDC"
  LinkPlacement = pos=(-111.125,-9.525,5.5) rot=(0,0.707107,0.707107;3.14159rad)
  LinkedObject = -> Shape
  Placement = pos=(-111.125,-9.525,5.5) rot=(0,0.707107,0.707107;3.14159rad)
FEATURE [App::Link] K_105_MX______________________________________1_______611CBFA4_2__ln_053  label="K_56_105_MX 轴标准键帽__¨¹_¡À__¡§1__¨¤_611DDBDC[2]"
  LinkPlacement = pos=(-120.125,-0.025,9.5) rot=(1,0,0;1.5708rad)
  LinkedObject = -> Shape001
  Placement = pos=(-120.125,-0.025,9.5) rot=(1,0,0;1.5708rad)
FEATURE [App::Link] K_105_cherry_mx_611CBFA4_ln_054  label="K_54_105_cherry mx_611DDB97"
  LinkPlacement = pos=(-149.225,-9.525,5.5) rot=(0,0.707107,0.707107;3.14159rad)
  LinkedObject = -> Shape
  Placement = pos=(-149.225,-9.525,5.5) rot=(0,0.707107,0.707107;3.14159rad)
FEATURE [App::Link] K_105_MX______________________________________1_______611CBFA4_2__ln_054  label="K_54_105_MX 轴标准键帽__¨¹_¡À__¡§1__¨¤_611DDB97[2]"
  LinkPlacement = pos=(-158.225,-0.025,9.5) rot=(1,0,0;1.5708rad)
  LinkedObject = -> Shape001
  Placement = pos=(-158.225,-0.025,9.5) rot=(1,0,0;1.5708rad)
FEATURE [App::Link] K_105_cherry_mx_611CBFA4_ln_055  label="K_53_105_cherry mx_611DDB82"
  LinkPlacement = pos=(155.575,-9.525,5.5) rot=(0,0.707107,0.707107;3.14159rad)
  LinkedObject = -> Shape
  Placement = pos=(155.575,-9.525,5.5) rot=(0,0.707107,0.707107;3.14159rad)
FEATURE [App::Link] K_105_MX______________________________________1_______611CBFA4_2__ln_055  label="K_53_105_MX 轴标准键帽__¨¹_¡À__¡§1__¨¤_611DDB82[2]"
  LinkPlacement = pos=(146.575,-0.025,9.5) rot=(1,0,0;1.5708rad)
  LinkedObject = -> Shape001
  Placement = pos=(146.575,-0.025,9.5) rot=(1,0,0;1.5708rad)
FEATURE [App::Link] K_105_cherry_mx_611CBFA4_ln_056  label="K_52_105_cherry mx_611DDB6D"
  LinkPlacement = pos=(-130.175,-9.525,5.5) rot=(0,0.707107,0.707107;3.14159rad)
  LinkedObject = -> Shape
  Placement = pos=(-130.175,-9.525,5.5) rot=(0,0.707107,0.707107;3.14159rad)
FEATURE [App::Link] K_105_MX______________________________________1_______611CBFA4_2__ln_056  label="K_52_105_MX 轴标准键帽__¨¹_¡À__¡§1__¨¤_611DDB6D[2]"
  LinkPlacement = pos=(-139.175,-0.025,9.5) rot=(1,0,0;1.5708rad)
  LinkedObject = -> Shape001
  Placement = pos=(-139.175,-0.025,9.5) rot=(1,0,0;1.5708rad)
FEATURE [App::Link] K_105_cherry_mx_611CBFA4_ln_057  label="K_51_105_cherry mx_611DDB58"
  LinkPlacement = pos=(155.575,9.525,5.5) rot=(0,0.707107,0.707107;3.14159rad)
  LinkedObject = -> Shape
  Placement = pos=(155.575,9.525,5.5) rot=(0,0.707107,0.707107;3.14159rad)
FEATURE [App::Link] K_105_MX______________________________________1_______611CBFA4_2__ln_057  label="K_51_105_MX 轴标准键帽__¨¹_¡À__¡§1__¨¤_611DDB58[2]"
  LinkPlacement = pos=(146.575,19.025,9.5) rot=(1,0,0;1.5708rad)
  LinkedObject = -> Shape001
  Placement = pos=(146.575,19.025,9.5) rot=(1,0,0;1.5708rad)
FEATURE [App::Link] K_105_cherry_mx_611CBFA4_ln_058  label="K_50_105_cherry mx_611DDB43"
  LinkPlacement = pos=(136.525,9.525,5.5) rot=(0,0.707107,0.707107;3.14159rad)
  LinkedObject = -> Shape
  Placement = pos=(136.525,9.525,5.5) rot=(0,0.707107,0.707107;3.14159rad)
FEATURE [App::Link] K_105_MX______________________________________1_______611CBFA4_2__ln_058  label="K_50_105_MX 轴标准键帽__¨¹_¡À__¡§1__¨¤_611DDB43[2]"
  LinkPlacement = pos=(127.525,19.025,9.5) rot=(1,0,0;1.5708rad)
  LinkedObject = -> Shape001
  Placement = pos=(127.525,19.025,9.5) rot=(1,0,0;1.5708rad)
FEATURE [App::Link] K_105_cherry_mx_611CBFA4_ln_059  label="K_49_105_cherry mx_611DDB2E"
  LinkPlacement = pos=(117.475,9.525,5.5) rot=(0,0.707107,0.707107;3.14159rad)
  LinkedObject = -> Shape
  Placement = pos=(117.475,9.525,5.5) rot=(0,0.707107,0.707107;3.14159rad)
FEATURE [App::Link] K_105_MX______________________________________1_______611CBFA4_2__ln_059  label="K_49_105_MX 轴标准键帽__¨¹_¡À__¡§1__¨¤_611DDB2E[2]"
  LinkPlacement = pos=(108.475,19.025,9.5) rot=(1,0,0;1.5708rad)
  LinkedObject = -> Shape001
  Placement = pos=(108.475,19.025,9.5) rot=(1,0,0;1.5708rad)
FEATURE [App::Link] K_105_cherry_mx_611CBFA4_ln_060  label="K_48_105_cherry mx_611DDB19"
  LinkPlacement = pos=(98.425,9.525,5.5) rot=(0,0.707107,0.707107;3.14159rad)
  LinkedObject = -> Shape
  Placement = pos=(98.425,9.525,5.5) rot=(0,0.707107,0.707107;3.14159rad)
FEATURE [App::Link] K_105_MX______________________________________1_______611CBFA4_2__ln_060  label="K_48_105_MX 轴标准键帽__¨¹_¡À__¡§1__¨¤_611DDB19[2]"
  LinkPlacement = pos=(89.425,19.025,9.5) rot=(1,0,0;1.5708rad)
  LinkedObject = -> Shape001
  Placement = pos=(89.425,19.025,9.5) rot=(1,0,0;1.5708rad)
FEATURE [App::Link] K_105_cherry_mx_611CBFA4_ln_061  label="K_47_105_cherry mx_611DDB04"
  LinkPlacement = pos=(79.375,9.525,5.5) rot=(0,0.707107,0.707107;3.14159rad)
  LinkedObject = -> Shape
  Placement = pos=(79.375,9.525,5.5) rot=(0,0.707107,0.707107;3.14159rad)
FEATURE [App::Link] K_105_MX______________________________________1_______611CBFA4_2__ln_061  label="K_47_105_MX 轴标准键帽__¨¹_¡À__¡§1__¨¤_611DDB04[2]"
  LinkPlacement = pos=(70.375,19.025,9.5) rot=(1,0,0;1.5708rad)
  LinkedObject = -> Shape001
  Placement = pos=(70.375,19.025,9.5) rot=(1,0,0;1.5708rad)
FEATURE [App::Link] K_105_cherry_mx_611CBFA4_ln_062  label="K_46_105_cherry mx_611DDAEF"
  LinkPlacement = pos=(60.325,9.525,5.5) rot=(0,0.707107,0.707107;3.14159rad)
  LinkedObject = -> Shape
  Placement = pos=(60.325,9.525,5.5) rot=(0,0.707107,0.707107;3.14159rad)
FEATURE [App::Link] K_105_MX______________________________________1_______611CBFA4_2__ln_062  label="K_46_105_MX 轴标准键帽__¨¹_¡À__¡§1__¨¤_611DDAEF[2]"
  LinkPlacement = pos=(51.325,19.025,9.5) rot=(1,0,0;1.5708rad)
  LinkedObject = -> Shape001
  Placement = pos=(51.325,19.025,9.5) rot=(1,0,0;1.5708rad)
FEATURE [App::Link] K_105_cherry_mx_611CBFA4_ln_063  label="K_45_105_cherry mx_611DDADA"
  LinkPlacement = pos=(41.275,9.525,5.5) rot=(0,0.707107,0.707107;3.14159rad)
  LinkedObject = -> Shape
  Placement = pos=(41.275,9.525,5.5) rot=(0,0.707107,0.707107;3.14159rad)
FEATURE [App::Link] K_105_MX______________________________________1_______611CBFA4_2__ln_063  label="K_45_105_MX 轴标准键帽__¨¹_¡À__¡§1__¨¤_611DDADA[2]"
  LinkPlacement = pos=(32.275,19.025,9.5) rot=(1,0,0;1.5708rad)
  LinkedObject = -> Shape001
  Placement = pos=(32.275,19.025,9.5) rot=(1,0,0;1.5708rad)
FEATURE [App::Link] K_105_cherry_mx_611CBFA4_ln_064  label="K_44_105_cherry mx_611DDAC5"
  LinkPlacement = pos=(22.225,9.525,5.5) rot=(0,0.707107,0.707107;3.14159rad)
  LinkedObject = -> Shape
  Placement = pos=(22.225,9.525,5.5) rot=(0,0.707107,0.707107;3.14159rad)
FEATURE [App::Link] K_105_MX______________________________________1_______611CBFA4_2__ln_064  label="K_44_105_MX 轴标准键帽__¨¹_¡À__¡§1__¨¤_611DDAC5[2]"
  LinkPlacement = pos=(13.225,19.025,9.5) rot=(1,0,0;1.5708rad)
  LinkedObject = -> Shape001
  Placement = pos=(13.225,19.025,9.5) rot=(1,0,0;1.5708rad)
FEATURE [App::Link] K_105_cherry_mx_611CBFA4_ln_065  label="K_43_105_cherry mx_611DDAB0"
  LinkPlacement = pos=(3.175,9.525,5.5) rot=(0,0.707107,0.707107;3.14159rad)
  LinkedObject = -> Shape
  Placement = pos=(3.175,9.525,5.5) rot=(0,0.707107,0.707107;3.14159rad)
FEATURE [App::Link] K_105_MX______________________________________1_______611CBFA4_2__ln_065  label="K_43_105_MX 轴标准键帽__¨¹_¡À__¡§1__¨¤_611DDAB0[2]"
  LinkPlacement = pos=(-5.825,19.025,9.5) rot=(1,0,0;1.5708rad)
  LinkedObject = -> Shape001
  Placement = pos=(-5.825,19.025,9.5) rot=(1,0,0;1.5708rad)
FEATURE [App::Link] K_105_cherry_mx_611CBFA4_ln_066  label="K_42_105_cherry mx_611DDA9B"
  LinkPlacement = pos=(-15.875,9.525,5.5) rot=(0,0.707107,0.707107;3.14159rad)
  LinkedObject = -> Shape
  Placement = pos=(-15.875,9.525,5.5) rot=(0,0.707107,0.707107;3.14159rad)
FEATURE [App::Link] K_105_MX______________________________________1_______611CBFA4_2__ln_066  label="K_42_105_MX 轴标准键帽__¨¹_¡À__¡§1__¨¤_611DDA9B[2]"
  LinkPlacement = pos=(-24.875,19.025,9.5) rot=(1,0,0;1.5708rad)
  LinkedObject = -> Shape001
  Placement = pos=(-24.875,19.025,9.5) rot=(1,0,0;1.5708rad)
FEATURE [App::Link] K_105_cherry_mx_611CBFA4_ln_067  label="K_41_105_cherry mx_611DDA86"
  LinkPlacement = pos=(-34.925,9.525,5.5) rot=(0,0.707107,0.707107;3.14159rad)
  LinkedObject = -> Shape
  Placement = pos=(-34.925,9.525,5.5) rot=(0,0.707107,0.707107;3.14159rad)
FEATURE [App::Link] K_105_MX______________________________________1_______611CBFA4_2__ln_067  label="K_41_105_MX 轴标准键帽__¨¹_¡À__¡§1__¨¤_611DDA86[2]"
  LinkPlacement = pos=(-43.925,19.025,9.5) rot=(1,0,0;1.5708rad)
  LinkedObject = -> Shape001
  Placement = pos=(-43.925,19.025,9.5) rot=(1,0,0;1.5708rad)
FEATURE [App::Link] K_105_cherry_mx_611CBFA4_ln_068  label="K_40_105_cherry mx_611DDA71"
  LinkPlacement = pos=(-53.975,9.525,5.5) rot=(0,0.707107,0.707107;3.14159rad)
  LinkedObject = -> Shape
  Placement = pos=(-53.975,9.525,5.5) rot=(0,0.707107,0.707107;3.14159rad)
FEATURE [App::Link] K_105_MX______________________________________1_______611CBFA4_2__ln_068  label="K_40_105_MX 轴标准键帽__¨¹_¡À__¡§1__¨¤_611DDA71[2]"
  LinkPlacement = pos=(-62.975,19.025,9.5) rot=(1,0,0;1.5708rad)
  LinkedObject = -> Shape001
  Placement = pos=(-62.975,19.025,9.5) rot=(1,0,0;1.5708rad)
FEATURE [App::Link] K_105_cherry_mx_611CBFA4_ln_069  label="K_39_105_cherry mx_611DDA5C"
  LinkPlacement = pos=(-73.025,9.525,5.5) rot=(0,0.707107,0.707107;3.14159rad)
  LinkedObject = -> Shape
  Placement = pos=(-73.025,9.525,5.5) rot=(0,0.707107,0.707107;3.14159rad)
FEATURE [App::Link] K_105_MX______________________________________1_______611CBFA4_2__ln_069  label="K_39_105_MX 轴标准键帽__¨¹_¡À__¡§1__¨¤_611DDA5C[2]"
  LinkPlacement = pos=(-82.025,19.025,9.5) rot=(1,0,0;1.5708rad)
  LinkedObject = -> Shape001
  Placement = pos=(-82.025,19.025,9.5) rot=(1,0,0;1.5708rad)
FEATURE [App::Link] K_105_cherry_mx_611CBFA4_ln_070  label="K_38_105_cherry mx_611DDA47"
  LinkPlacement = pos=(-92.075,9.525,5.5) rot=(0,0.707107,0.707107;3.14159rad)
  LinkedObject = -> Shape
  Placement = pos=(-92.075,9.525,5.5) rot=(0,0.707107,0.707107;3.14159rad)
FEATURE [App::Link] K_105_MX______________________________________1_______611CBFA4_2__ln_070  label="K_38_105_MX 轴标准键帽__¨¹_¡À__¡§1__¨¤_611DDA47[2]"
  LinkPlacement = pos=(-101.075,19.025,9.5) rot=(1,0,0;1.5708rad)
  LinkedObject = -> Shape001
  Placement = pos=(-101.075,19.025,9.5) rot=(1,0,0;1.5708rad)
FEATURE [App::Link] K_105_cherry_mx_611CBFA4_ln_071  label="K_37_105_cherry mx_611DDA32"
  LinkPlacement = pos=(-111.125,9.525,5.5) rot=(0,0.707107,0.707107;3.14159rad)
  LinkedObject = -> Shape
  Placement = pos=(-111.125,9.525,5.5) rot=(0,0.707107,0.707107;3.14159rad)
FEATURE [App::Link] K_105_MX______________________________________1_______611CBFA4_2__ln_071  label="K_37_105_MX 轴标准键帽__¨¹_¡À__¡§1__¨¤_611DDA32[2]"
  LinkPlacement = pos=(-120.125,19.025,9.5) rot=(1,0,0;1.5708rad)
  LinkedObject = -> Shape001
  Placement = pos=(-120.125,19.025,9.5) rot=(1,0,0;1.5708rad)
FEATURE [App::Link] K_105_cherry_mx_611CBFA4_ln_072  label="K_35_105_cherry mx_611DD9ED"
  LinkPlacement = pos=(-149.225,9.525,5.5) rot=(0,0.707107,0.707107;3.14159rad)
  LinkedObject = -> Shape
  Placement = pos=(-149.225,9.525,5.5) rot=(0,0.707107,0.707107;3.14159rad)
FEATURE [App::Link] K_105_MX______________________________________1_______611CBFA4_2__ln_072  label="K_35_105_MX 轴标准键帽__¨¹_¡À__¡§1__¨¤_611DD9ED[2]"
  LinkPlacement = pos=(-158.225,19.025,9.5) rot=(1,0,0;1.5708rad)
  LinkedObject = -> Shape001
  Placement = pos=(-158.225,19.025,9.5) rot=(1,0,0;1.5708rad)
FEATURE [App::Link] K_105_cherry_mx_611CBFA4_ln_073  label="K_34_105_cherry mx_611DD9D8"
  LinkPlacement = pos=(-130.175,9.525,5.5) rot=(0,0.707107,0.707107;3.14159rad)
  LinkedObject = -> Shape
  Placement = pos=(-130.175,9.525,5.5) rot=(0,0.707107,0.707107;3.14159rad)
FEATURE [App::Link] K_105_MX______________________________________1_______611CBFA4_2__ln_073  label="K_34_105_MX 轴标准键帽__¨¹_¡À__¡§1__¨¤_611DD9D8[2]"
  LinkPlacement = pos=(-139.175,19.025,9.5) rot=(1,0,0;1.5708rad)
  LinkedObject = -> Shape001
  Placement = pos=(-139.175,19.025,9.5) rot=(1,0,0;1.5708rad)
FEATURE [App::Link] K_105_cherry_mx_611CBFA4_ln_074  label="K_31_105_cherry mx_611DD993"
  LinkPlacement = pos=(117.475,28.575,5.5) rot=(0,0.707107,0.707107;3.14159rad)
  LinkedObject = -> Shape
  Placement = pos=(117.475,28.575,5.5) rot=(0,0.707107,0.707107;3.14159rad)
FEATURE [App::Link] K_105_MX______________________________________1_______611CBFA4_2__ln_074  label="K_31_105_MX 轴标准键帽__¨¹_¡À__¡§1__¨¤_611DD993[2]"
  LinkPlacement = pos=(108.475,38.075,9.5) rot=(1,0,0;1.5708rad)
  LinkedObject = -> Shape001
  Placement = pos=(108.475,38.075,9.5) rot=(1,0,0;1.5708rad)
FEATURE [App::Link] K_105_cherry_mx_611CBFA4_ln_075  label="K_30_105_cherry mx_611DD97E"
  LinkPlacement = pos=(98.425,28.575,5.5) rot=(0,0.707107,0.707107;3.14159rad)
  LinkedObject = -> Shape
  Placement = pos=(98.425,28.575,5.5) rot=(0,0.707107,0.707107;3.14159rad)
FEATURE [App::Link] K_105_MX______________________________________1_______611CBFA4_2__ln_075  label="K_30_105_MX 轴标准键帽__¨¹_¡À__¡§1__¨¤_611DD97E[2]"
  LinkPlacement = pos=(89.425,38.075,9.5) rot=(1,0,0;1.5708rad)
  LinkedObject = -> Shape001
  Placement = pos=(89.425,38.075,9.5) rot=(1,0,0;1.5708rad)
FEATURE [App::Link] K_105_cherry_mx_611CBFA4_ln_076  label="K_29_105_cherry mx_611DD969"
  LinkPlacement = pos=(79.375,28.575,5.5) rot=(0,0.707107,0.707107;3.14159rad)
  LinkedObject = -> Shape
  Placement = pos=(79.375,28.575,5.5) rot=(0,0.707107,0.707107;3.14159rad)
FEATURE [App::Link] K_105_MX______________________________________1_______611CBFA4_2__ln_076  label="K_29_105_MX 轴标准键帽__¨¹_¡À__¡§1__¨¤_611DD969[2]"
  LinkPlacement = pos=(70.375,38.075,9.5) rot=(1,0,0;1.5708rad)
  LinkedObject = -> Shape001
  Placement = pos=(70.375,38.075,9.5) rot=(1,0,0;1.5708rad)
FEATURE [App::Link] K_105_cherry_mx_611CBFA4_ln_077  label="K_28_105_cherry mx_611DD954"
  LinkPlacement = pos=(60.325,28.575,5.5) rot=(0,0.707107,0.707107;3.14159rad)
  LinkedObject = -> Shape
  Placement = pos=(60.325,28.575,5.5) rot=(0,0.707107,0.707107;3.14159rad)
FEATURE [App::Link] K_105_MX______________________________________1_______611CBFA4_2__ln_077  label="K_28_105_MX 轴标准键帽__¨¹_¡À__¡§1__¨¤_611DD954[2]"
  LinkPlacement = pos=(51.325,38.075,9.5) rot=(1,0,0;1.5708rad)
  LinkedObject = -> Shape001
  Placement = pos=(51.325,38.075,9.5) rot=(1,0,0;1.5708rad)
FEATURE [App::Link] K_105_cherry_mx_611CBFA4_ln_078  label="K_27_105_cherry mx_611DD93F"
  LinkPlacement = pos=(41.275,28.575,5.5) rot=(0,0.707107,0.707107;3.14159rad)
  LinkedObject = -> Shape
  Placement = pos=(41.275,28.575,5.5) rot=(0,0.707107,0.707107;3.14159rad)
FEATURE [App::Link] K_105_MX______________________________________1_______611CBFA4_2__ln_078  label="K_27_105_MX 轴标准键帽__¨¹_¡À__¡§1__¨¤_611DD93F[2]"
  LinkPlacement = pos=(32.275,38.075,9.5) rot=(1,0,0;1.5708rad)
  LinkedObject = -> Shape001
  Placement = pos=(32.275,38.075,9.5) rot=(1,0,0;1.5708rad)
FEATURE [App::Link] K_105_cherry_mx_611CBFA4_ln_079  label="K_26_105_cherry mx_611DD92A"
  LinkPlacement = pos=(22.225,28.575,5.5) rot=(0,0.707107,0.707107;3.14159rad)
  LinkedObject = -> Shape
  Placement = pos=(22.225,28.575,5.5) rot=(0,0.707107,0.707107;3.14159rad)
FEATURE [App::Link] K_105_MX______________________________________1_______611CBFA4_2__ln_079  label="K_26_105_MX 轴标准键帽__¨¹_¡À__¡§1__¨¤_611DD92A[2]"
  LinkPlacement = pos=(13.225,38.075,9.5) rot=(1,0,0;1.5708rad)
  LinkedObject = -> Shape001
  Placement = pos=(13.225,38.075,9.5) rot=(1,0,0;1.5708rad)
FEATURE [App::Link] K_105_cherry_mx_611CBFA4_ln_080  label="K_25_105_cherry mx_611DD915"
  LinkPlacement = pos=(3.175,28.575,5.5) rot=(0,0.707107,0.707107;3.14159rad)
  LinkedObject = -> Shape
  Placement = pos=(3.175,28.575,5.5) rot=(0,0.707107,0.707107;3.14159rad)
FEATURE [App::Link] K_105_MX______________________________________1_______611CBFA4_2__ln_080  label="K_25_105_MX 轴标准键帽__¨¹_¡À__¡§1__¨¤_611DD915[2]"
  LinkPlacement = pos=(-5.825,38.075,9.5) rot=(1,0,0;1.5708rad)
  LinkedObject = -> Shape001
  Placement = pos=(-5.825,38.075,9.5) rot=(1,0,0;1.5708rad)
FEATURE [App::Link] K_105_cherry_mx_611CBFA4_ln_081  label="K_24_105_cherry mx_611DD900"
  LinkPlacement = pos=(-15.875,28.575,5.5) rot=(0,0.707107,0.707107;3.14159rad)
  LinkedObject = -> Shape
  Placement = pos=(-15.875,28.575,5.5) rot=(0,0.707107,0.707107;3.14159rad)
FEATURE [App::Link] K_105_MX______________________________________1_______611CBFA4_2__ln_081  label="K_24_105_MX 轴标准键帽__¨¹_¡À__¡§1__¨¤_611DD900[2]"
  LinkPlacement = pos=(-24.875,38.075,9.5) rot=(1,0,0;1.5708rad)
  LinkedObject = -> Shape001
  Placement = pos=(-24.875,38.075,9.5) rot=(1,0,0;1.5708rad)
FEATURE [App::Link] K_105_cherry_mx_611CBFA4_ln_082  label="K_23_105_cherry mx_611DD8EB"
  LinkPlacement = pos=(-34.925,28.575,5.5) rot=(0,0.707107,0.707107;3.14159rad)
  LinkedObject = -> Shape
  Placement = pos=(-34.925,28.575,5.5) rot=(0,0.707107,0.707107;3.14159rad)
FEATURE [App::Link] K_105_MX______________________________________1_______611CBFA4_2__ln_082  label="K_23_105_MX 轴标准键帽__¨¹_¡À__¡§1__¨¤_611DD8EB[2]"
  LinkPlacement = pos=(-43.925,38.075,9.5) rot=(1,0,0;1.5708rad)
  LinkedObject = -> Shape001
  Placement = pos=(-43.925,38.075,9.5) rot=(1,0,0;1.5708rad)
FEATURE [App::Link] K_105_cherry_mx_611CBFA4_ln_083  label="K_22_105_cherry mx_611DD8D6"
  LinkPlacement = pos=(-53.975,28.575,5.5) rot=(0,0.707107,0.707107;3.14159rad)
  LinkedObject = -> Shape
  Placement = pos=(-53.975,28.575,5.5) rot=(0,0.707107,0.707107;3.14159rad)
FEATURE [App::Link] K_105_MX______________________________________1_______611CBFA4_2__ln_083  label="K_22_105_MX 轴标准键帽__¨¹_¡À__¡§1__¨¤_611DD8D6[2]"
  LinkPlacement = pos=(-62.975,38.075,9.5) rot=(1,0,0;1.5708rad)
  LinkedObject = -> Shape001
  Placement = pos=(-62.975,38.075,9.5) rot=(1,0,0;1.5708rad)
FEATURE [App::Link] K_105_cherry_mx_611CBFA4_ln_084  label="K_21_105_cherry mx_611DD8C1"
  LinkPlacement = pos=(-73.025,28.575,5.5) rot=(0,0.707107,0.707107;3.14159rad)
  LinkedObject = -> Shape
  Placement = pos=(-73.025,28.575,5.5) rot=(0,0.707107,0.707107;3.14159rad)
FEATURE [App::Link] K_105_MX______________________________________1_______611CBFA4_2__ln_084  label="K_21_105_MX 轴标准键帽__¨¹_¡À__¡§1__¨¤_611DD8C1[2]"
  LinkPlacement = pos=(-82.025,38.075,9.5) rot=(1,0,0;1.5708rad)
  LinkedObject = -> Shape001
  Placement = pos=(-82.025,38.075,9.5) rot=(1,0,0;1.5708rad)
FEATURE [App::Link] K_105_cherry_mx_611CBFA4_ln_085  label="K_20_105_cherry mx_611DD8AC"
  LinkPlacement = pos=(-92.075,28.575,5.5) rot=(0,0.707107,0.707107;3.14159rad)
  LinkedObject = -> Shape
  Placement = pos=(-92.075,28.575,5.5) rot=(0,0.707107,0.707107;3.14159rad)
FEATURE [App::Link] K_105_MX______________________________________1_______611CBFA4_2__ln_085  label="K_20_105_MX 轴标准键帽__¨¹_¡À__¡§1__¨¤_611DD8AC[2]"
  LinkPlacement = pos=(-101.075,38.075,9.5) rot=(1,0,0;1.5708rad)
  LinkedObject = -> Shape001
  Placement = pos=(-101.075,38.075,9.5) rot=(1,0,0;1.5708rad)
FEATURE [App::Link] K_105_cherry_mx_611CBFA4_ln_086  label="K_19_105_cherry mx_611DD897"
  LinkPlacement = pos=(-111.125,28.575,5.5) rot=(0,0.707107,0.707107;3.14159rad)
  LinkedObject = -> Shape
  Placement = pos=(-111.125,28.575,5.5) rot=(0,0.707107,0.707107;3.14159rad)
FEATURE [App::Link] K_105_MX______________________________________1_______611CBFA4_2__ln_086  label="K_19_105_MX 轴标准键帽__¨¹_¡À__¡§1__¨¤_611DD897[2]"
  LinkPlacement = pos=(-120.125,38.075,9.5) rot=(1,0,0;1.5708rad)
  LinkedObject = -> Shape001
  Placement = pos=(-120.125,38.075,9.5) rot=(1,0,0;1.5708rad)
FEATURE [App::Link] K_105_cherry_mx_611CBFA4_ln_087  label="K_18_105_cherry mx_611DD882"
  LinkPlacement = pos=(-130.175,28.575,5.5) rot=(0,0.707107,0.707107;3.14159rad)
  LinkedObject = -> Shape
  Placement = pos=(-130.175,28.575,5.5) rot=(0,0.707107,0.707107;3.14159rad)
FEATURE [App::Link] K_105_MX______________________________________1_______611CBFA4_2__ln_087  label="K_18_105_MX 轴标准键帽__¨¹_¡À__¡§1__¨¤_611DD882[2]"
  LinkPlacement = pos=(-139.175,38.075,9.5) rot=(1,0,0;1.5708rad)
  LinkedObject = -> Shape001
  Placement = pos=(-139.175,38.075,9.5) rot=(1,0,0;1.5708rad)
FEATURE [App::Link] K_105_cherry_mx_611CBFA4_ln_088  label="K_17_105_cherry mx_611DD86D"
  LinkPlacement = pos=(136.525,28.575,5.5) rot=(0,0.707107,0.707107;3.14159rad)
  LinkedObject = -> Shape
  Placement = pos=(136.525,28.575,5.5) rot=(0,0.707107,0.707107;3.14159rad)
FEATURE [App::Link] K_105_MX______________________________________1_______611CBFA4_2__ln_088  label="K_17_105_MX 轴标准键帽__¨¹_¡À__¡§1__¨¤_611DD86D[2]"
  LinkPlacement = pos=(127.525,38.075,9.5) rot=(1,0,0;1.5708rad)
  LinkedObject = -> Shape001
  Placement = pos=(127.525,38.075,9.5) rot=(1,0,0;1.5708rad)
FEATURE [App::Link] K_105_cherry_mx_611CBFA4_ln_089  label="K_16_105_cherry mx_611DD858"
  LinkPlacement = pos=(117.475,47.625,5.5) rot=(0,0.707107,0.707107;3.14159rad)
  LinkedObject = -> Shape
  Placement = pos=(117.475,47.625,5.5) rot=(0,0.707107,0.707107;3.14159rad)
FEATURE [App::Link] K_105_MX______________________________________1_______611CBFA4_2__ln_089  label="K_16_105_MX 轴标准键帽__¨¹_¡À__¡§1__¨¤_611DD858[2]"
  LinkPlacement = pos=(108.475,57.125,9.5) rot=(1,0,0;1.5708rad)
  LinkedObject = -> Shape001
  Placement = pos=(108.475,57.125,9.5) rot=(1,0,0;1.5708rad)
FEATURE [App::Link] K_105_cherry_mx_611CBFA4_ln_090  label="K_15_105_cherry mx_611DD843"
  LinkPlacement = pos=(98.425,47.625,5.5) rot=(0,0.707107,0.707107;3.14159rad)
  LinkedObject = -> Shape
  Placement = pos=(98.425,47.625,5.5) rot=(0,0.707107,0.707107;3.14159rad)
FEATURE [App::Link] K_105_MX______________________________________1_______611CBFA4_2__ln_090  label="K_15_105_MX 轴标准键帽__¨¹_¡À__¡§1__¨¤_611DD843[2]"
  LinkPlacement = pos=(89.425,57.125,9.5) rot=(1,0,0;1.5708rad)
  LinkedObject = -> Shape001
  Placement = pos=(89.425,57.125,9.5) rot=(1,0,0;1.5708rad)
FEATURE [App::Link] K_105_cherry_mx_611CBFA4_ln_091  label="K_14_105_cherry mx_611DD82E"
  LinkPlacement = pos=(79.375,47.625,5.5) rot=(0,0.707107,0.707107;3.14159rad)
  LinkedObject = -> Shape
  Placement = pos=(79.375,47.625,5.5) rot=(0,0.707107,0.707107;3.14159rad)
FEATURE [App::Link] K_105_MX______________________________________1_______611CBFA4_2__ln_091  label="K_14_105_MX 轴标准键帽__¨¹_¡À__¡§1__¨¤_611DD82E[2]"
  LinkPlacement = pos=(70.375,57.125,9.5) rot=(1,0,0;1.5708rad)
  LinkedObject = -> Shape001
  Placement = pos=(70.375,57.125,9.5) rot=(1,0,0;1.5708rad)
FEATURE [App::Link] K_105_cherry_mx_611CBFA4_ln_092  label="K_13_105_cherry mx_611DD819"
  LinkPlacement = pos=(60.325,47.625,5.5) rot=(0,0.707107,0.707107;3.14159rad)
  LinkedObject = -> Shape
  Placement = pos=(60.325,47.625,5.5) rot=(0,0.707107,0.707107;3.14159rad)
FEATURE [App::Link] K_105_MX______________________________________1_______611CBFA4_2__ln_092  label="K_13_105_MX 轴标准键帽__¨¹_¡À__¡§1__¨¤_611DD819[2]"
  LinkPlacement = pos=(51.325,57.125,9.5) rot=(1,0,0;1.5708rad)
  LinkedObject = -> Shape001
  Placement = pos=(51.325,57.125,9.5) rot=(1,0,0;1.5708rad)
FEATURE [App::Link] K_105_cherry_mx_611CBFA4_ln_093  label="K_12_105_cherry mx_611DD804"
  LinkPlacement = pos=(41.275,47.625,5.5) rot=(0,0.707107,0.707107;3.14159rad)
  LinkedObject = -> Shape
  Placement = pos=(41.275,47.625,5.5) rot=(0,0.707107,0.707107;3.14159rad)
FEATURE [App::Link] K_105_MX______________________________________1_______611CBFA4_2__ln_093  label="K_12_105_MX 轴标准键帽__¨¹_¡À__¡§1__¨¤_611DD804[2]"
  LinkPlacement = pos=(32.275,57.125,9.5) rot=(1,0,0;1.5708rad)
  LinkedObject = -> Shape001
  Placement = pos=(32.275,57.125,9.5) rot=(1,0,0;1.5708rad)
FEATURE [App::Link] K_105_cherry_mx_611CBFA4_ln_094  label="K_11_105_cherry mx_611DD7EF"
  LinkPlacement = pos=(22.225,47.625,5.5) rot=(0,0.707107,0.707107;3.14159rad)
  LinkedObject = -> Shape
  Placement = pos=(22.225,47.625,5.5) rot=(0,0.707107,0.707107;3.14159rad)
FEATURE [App::Link] K_105_MX______________________________________1_______611CBFA4_2__ln_094  label="K_11_105_MX 轴标准键帽__¨¹_¡À__¡§1__¨¤_611DD7EF[2]"
  LinkPlacement = pos=(13.225,57.125,9.5) rot=(1,0,0;1.5708rad)
  LinkedObject = -> Shape001
  Placement = pos=(13.225,57.125,9.5) rot=(1,0,0;1.5708rad)
FEATURE [App::Link] K_105_cherry_mx_611CBFA4_ln_095  label="K_10_105_cherry mx_611DD7DA"
  LinkPlacement = pos=(3.175,47.625,5.5) rot=(0,0.707107,0.707107;3.14159rad)
  LinkedObject = -> Shape
  Placement = pos=(3.175,47.625,5.5) rot=(0,0.707107,0.707107;3.14159rad)
FEATURE [App::Link] K_105_MX______________________________________1_______611CBFA4_2__ln_095  label="K_10_105_MX 轴标准键帽__¨¹_¡À__¡§1__¨¤_611DD7DA[2]"
  LinkPlacement = pos=(-5.825,57.125,9.5) rot=(1,0,0;1.5708rad)
  LinkedObject = -> Shape001
  Placement = pos=(-5.825,57.125,9.5) rot=(1,0,0;1.5708rad)
FEATURE [App::Link] K_105_cherry_mx_611CBFA4_ln_096  label="K_104_105_cherry mx_611CBF8B"
  LinkPlacement = pos=(79.375,-47.6255,5.5) rot=(0,0.707107,0.707107;3.14159rad)
  LinkedObject = -> Shape
  Placement = pos=(79.375,-47.6255,5.5) rot=(0,0.707107,0.707107;3.14159rad)
FEATURE [App::Link] K_105_cherry_mx_611CBFA4_ln_097  label="K_96_105_cherry mx_611CBF76"
  LinkPlacement = pos=(-73.025,-47.6255,5.5) rot=(0,0.707107,0.707107;3.14159rad)
  LinkedObject = -> Shape
  Placement = pos=(-73.025,-47.6255,5.5) rot=(0,0.707107,0.707107;3.14159rad)
FEATURE [Part::Feature] Part__Feature  label="mx Stabilizer base 16828"
  shape: bbox 6.802 x 10.1 x 19.67 mm, 163 faces (baked)
FEATURE [Part::Feature] Part__Feature001  label="mx Stabilizer key 16828"
  Placement = pos=(0,8.1,0) rot=(0,0,1;0rad)
  shape: bbox 4.6 x 11.96 x 8.302 mm, 299 faces (baked)
FEATURE [Part::Feature] Part__Feature002  label="metal stick 16828"
  Placement = pos=(11.95,4.09188,-1.57187) rot=(1,0,0;0.574181rad)
  shape: bbox 25.8 x 7.719 x 10.9 mm, 12 faces (baked)
FEATURE [Part::Feature] Part__Feature003  label="mx Stabilizer base 16829"
  Placement = pos=(23.9,-1.1e-15,-2e-16) rot=(0,0,1;0rad)
  shape: bbox 6.802 x 10.1 x 19.67 mm, 163 faces (baked)
FEATURE [Part::Feature] Part__Feature004  label="mx Stabilizer key 16829"
  Placement = pos=(23.9,8.1,0) rot=(0,0,1;0rad)
  shape: bbox 4.6 x 11.96 x 8.302 mm, 299 faces (baked)
FEATURE [App::Part] Stabilizer___open  label="K_89_Stabilizer - open_611CBF5D"
  Group = -> [Part__Feature,Part__Feature001,Part__Feature002,Part__Feature003,Part__Feature004]
  Origin = -> Origin008
  Placement = pos=(134.05,-28.5755,3.5) rot=(1,0,0;1.5708rad)
FEATURE [App::Link] K_105_cherry_mx_611CBFA4_ln_098  label="K_89_105_cherry mx_611CBF5D[2]"
  LinkPlacement = pos=(146.05,-28.5755,5.5) rot=(0,0.707107,0.707107;3.14159rad)
  LinkedObject = -> Shape
  Placement = pos=(146.05,-28.5755,5.5) rot=(0,0.707107,0.707107;3.14159rad)
FEATURE [App::Link] K_89_Stabilizer___open_611CBF5D_ln_  label="K_74_89_Stabilizer - open_611CBF44"
  LinkPlacement = pos=(-151.7,-28.5755,3.5) rot=(1,0,0;1.5708rad)
  LinkedObject = -> Stabilizer___open
  Placement = pos=(-151.7,-28.5755,3.5) rot=(1,0,0;1.5708rad)
FEATURE [App::Link] K_105_cherry_mx_611CBFA4_ln_099  label="K_74_105_cherry mx_611CBF44[2]"
  LinkPlacement = pos=(-139.7,-28.5755,5.5) rot=(0,0.707107,0.707107;3.14159rad)
  LinkedObject = -> Shape
  Placement = pos=(-139.7,-28.5755,5.5) rot=(0,0.707107,0.707107;3.14159rad)
FEATURE [App::Link] K_89_Stabilizer___open_611CBF5D_ln_001  label="K_70_89_Stabilizer - open_611CBF2B"
  LinkPlacement = pos=(134.05,-9.525,3.5) rot=(1,0,0;1.5708rad)
  LinkedObject = -> Stabilizer___open
  Placement = pos=(134.05,-9.525,3.5) rot=(1,0,0;1.5708rad)
FEATURE [App::Link] K_105_cherry_mx_611CBFA4_ln_100  label="K_70_105_cherry mx_611CBF2B[2]"
  LinkPlacement = pos=(146.05,-9.525,5.5) rot=(0,0.707107,0.707107;3.14159rad)
  LinkedObject = -> Shape
  Placement = pos=(146.05,-9.525,5.5) rot=(0,0.707107,0.707107;3.14159rad)
FEATURE [App::Link] K_89_Stabilizer___open_611CBF5D_ln_002  label="K_55_89_Stabilizer - open_611CBF12"
  LinkPlacement = pos=(-151.7,-9.525,3.5) rot=(1,0,0;1.5708rad)
  LinkedObject = -> Stabilizer___open
  Placement = pos=(-151.7,-9.525,3.5) rot=(1,0,0;1.5708rad)
FEATURE [App::Link] K_105_cherry_mx_611CBFA4_ln_101  label="K_55_105_cherry mx_611CBF12[2]"
  LinkPlacement = pos=(-139.7,-9.525,5.5) rot=(0,0.707107,0.707107;3.14159rad)
  LinkedObject = -> Shape
  Placement = pos=(-139.7,-9.525,5.5) rot=(0,0.707107,0.707107;3.14159rad)
FEATURE [App::Link] K_89_Stabilizer___open_611CBF5D_ln_003  label="K_36_89_Stabilizer - open_611CBEF9"
  LinkPlacement = pos=(-151.7,9.525,3.5) rot=(1,0,0;1.5708rad)
  LinkedObject = -> Stabilizer___open
  Placement = pos=(-151.7,9.525,3.5) rot=(1,0,0;1.5708rad)
FEATURE [App::Link] K_105_cherry_mx_611CBFA4_ln_102  label="K_36_105_cherry mx_611CBEF9[2]"
  LinkPlacement = pos=(-139.7,9.525,5.5) rot=(0,0.707107,0.707107;3.14159rad)
  LinkedObject = -> Shape
  Placement = pos=(-139.7,9.525,5.5) rot=(0,0.707107,0.707107;3.14159rad)
FEATURE [App::Link] K_89_Stabilizer___open_611CBF5D_ln_004  label="K_32_89_Stabilizer - open_611CBEE0"
  LinkPlacement = pos=(115,28.575,3.5) rot=(1,0,0;1.5708rad)
  LinkedObject = -> Stabilizer___open
  Placement = pos=(115,28.575,3.5) rot=(1,0,0;1.5708rad)
FEATURE [App::Link] K_105_cherry_mx_611CBFA4_ln_103  label="K_32_105_cherry mx_611CBEE0[2]"
  LinkPlacement = pos=(127,28.575,5.5) rot=(0,0.707107,0.707107;3.14159rad)
  LinkedObject = -> Shape
  Placement = pos=(127,28.575,5.5) rot=(0,0.707107,0.707107;3.14159rad)
FEATURE [Part::Feature] Part__Feature005  label="SHELL"
  shape: bbox 2.5 x 2.5 x 0.6 mm, 1 faces, 0 solids (baked)
FEATURE [Part::Feature] Part__Feature006  label="SOLID"
  shape: bbox 5.88 x 2.8 x 1.6 mm, 77 faces (baked)
FEATURE [App::Part] _228_reverse_mount_led_v1  label="D24_3228_reverse_mount_led v1_611CB79E[2]"
  Group = -> [Part__Feature005,Part__Feature006]
  Origin = -> Origin009
  Placement = pos=(108.418,-42.1405,-1.5) rot=(0,0,1;1.5708rad)
FEATURE [App::Link] D24_3228_reverse_mount_led_v1_611CB79E_2__ln_  label="D23_3228_reverse_mount_led v1_611CB784[2]"
  LinkPlacement = pos=(51.307,-42.3555,-1.5) rot=(0,0,1;1.5708rad)
  LinkedObject = -> _228_reverse_mount_led_v1
  Placement = pos=(51.307,-42.3555,-1.5) rot=(0,0,1;1.5708rad)
FEATURE [App::Link] D24_3228_reverse_mount_led_v1_611CB79E_2__ln_001  label="D22_3228_reverse_mount_led v1_611CB76A[2]"
  LinkPlacement = pos=(-43.727,-42.1405,-1.5) rot=(0,0,1;1.5708rad)
  LinkedObject = -> _228_reverse_mount_led_v1
  Placement = pos=(-43.727,-42.1405,-1.5) rot=(0,0,1;1.5708rad)
FEATURE [App::Link] D24_3228_reverse_mount_led_v1_611CB79E_2__ln_002  label="D21_3228_reverse_mount_led v1_611CB750[2]"
  LinkPlacement = pos=(-100.846,-42.1715,-1.5) rot=(0,0,1;1.5708rad)
  LinkedObject = -> _228_reverse_mount_led_v1
  Placement = pos=(-100.846,-42.1715,-1.5) rot=(0,0,1;1.5708rad)
FEATURE [Part::Feature] Shape002  label="R7_R_0603_1608Metric_611CC01B"
  Placement = pos=(-146.018,21.2407,-1.6) rot=(0,1,0;3.14159rad)
  shape: bbox 1.6 x 0.8 x 0.45 mm, 26 faces (baked)
FEATURE [App::Link] R7_R_0603_1608Metric_611CC01B_ln_  label="R7_R_0603_1608Metric_611CC01B[2]"
  LinkPlacement = pos=(-146.018,21.2407,-1.6) rot=(0,1,0;3.14159rad)
  LinkedObject = -> Shape002
  Placement = pos=(-146.018,21.2407,-1.6) rot=(0,1,0;3.14159rad)
FEATURE [App::Link] R7_R_0603_1608Metric_611CC01B_ln_001  label="R6_R_0603_1608Metric_611CC011"
  LinkPlacement = pos=(-158.178,36.5125,-1.6) rot=(0.707107,0.707107,0;3.14159rad)
  LinkedObject = -> Shape002
  Placement = pos=(-158.178,36.5125,-1.6) rot=(0.707107,0.707107,0;3.14159rad)
FEATURE [App::Link] R7_R_0603_1608Metric_611CC01B_ln_002  label="R6_R_0603_1608Metric_611CC011[2]"
  LinkPlacement = pos=(-158.178,36.5125,-1.6) rot=(0.707107,0.707107,0;3.14159rad)
  LinkedObject = -> Shape002
  Placement = pos=(-158.178,36.5125,-1.6) rot=(0.707107,0.707107,0;3.14159rad)
FEATURE [App::Link] R7_R_0603_1608Metric_611CC01B_ln_003  label="R4_R_0603_1608Metric_611CBFF6"
  LinkPlacement = pos=(-155.257,22.1933,-1.6) rot=(1,0,0;3.14159rad)
  LinkedObject = -> Shape002
  Placement = pos=(-155.257,22.1933,-1.6) rot=(1,0,0;3.14159rad)
FEATURE [App::Link] R7_R_0603_1608Metric_611CC01B_ln_004  label="R4_R_0603_1608Metric_611CBFF6[2]"
  LinkPlacement = pos=(-155.257,22.1933,-1.6) rot=(1,0,0;3.14159rad)
  LinkedObject = -> Shape002
  Placement = pos=(-155.257,22.1933,-1.6) rot=(1,0,0;3.14159rad)
FEATURE [App::Link] R7_R_0603_1608Metric_611CC01B_ln_005  label="R3_R_0603_1608Metric_611CBFEC"
  LinkPlacement = pos=(-155.257,23.7807,-1.6) rot=(0,1,0;3.14159rad)
  LinkedObject = -> Shape002
  Placement = pos=(-155.257,23.7807,-1.6) rot=(0,1,0;3.14159rad)
FEATURE [App::Link] R7_R_0603_1608Metric_611CC01B_ln_006  label="R3_R_0603_1608Metric_611CBFEC[2]"
  LinkPlacement = pos=(-155.257,23.7807,-1.6) rot=(0,1,0;3.14159rad)
  LinkedObject = -> Shape002
  Placement = pos=(-155.257,23.7807,-1.6) rot=(0,1,0;3.14159rad)
FEATURE [App::Link] R7_R_0603_1608Metric_611CC01B_ln_007  label="R2_R_0603_1608Metric_611CBFE2"
  LinkPlacement = pos=(-95.758,38.0365,-1.6) rot=(-0.707107,0.707107,0;3.14159rad)
  LinkedObject = -> Shape002
  Placement = pos=(-95.758,38.0365,-1.6) rot=(-0.707107,0.707107,0;3.14159rad)
FEATURE [App::Link] R7_R_0603_1608Metric_611CC01B_ln_008  label="R2_R_0603_1608Metric_611CBFE2[2]"
  LinkPlacement = pos=(-95.758,38.0365,-1.6) rot=(-0.707107,0.707107,0;3.14159rad)
  LinkedObject = -> Shape002
  Placement = pos=(-95.758,38.0365,-1.6) rot=(-0.707107,0.707107,0;3.14159rad)
FEATURE [App::Link] R7_R_0603_1608Metric_611CC01B_ln_009  label="R1_R_0603_1608Metric_611CBFD8"
  LinkPlacement = pos=(-98.425,35.3695,-1.6) rot=(0,1,0;3.14159rad)
  LinkedObject = -> Shape002
  Placement = pos=(-98.425,35.3695,-1.6) rot=(0,1,0;3.14159rad)
FEATURE [App::Link] R7_R_0603_1608Metric_611CC01B_ln_010  label="R1_R_0603_1608Metric_611CBFD8[2]"
  LinkPlacement = pos=(-98.425,35.3695,-1.6) rot=(0,1,0;3.14159rad)
  LinkedObject = -> Shape002
  Placement = pos=(-98.425,35.3695,-1.6) rot=(0,1,0;3.14159rad)
FEATURE [Part::Feature] Shape003  label="C37_C_0603_1608Metric_611CB56A"
  Placement = pos=(109.156,-46.4185,-1.6) rot=(0.707107,0.707107,0;3.14159rad)
  shape: bbox 0.8 x 1.6 x 0.8 mm, 28 faces (baked)
FEATURE [App::Link] C37_C_0603_1608Metric_611CB56A_ln_  label="C36_C_0603_1608Metric_611CB560"
  LinkPlacement = pos=(52.045,-46.6345,-1.6) rot=(0.707107,0.707107,0;3.14159rad)
  LinkedObject = -> Shape003
  Placement = pos=(52.045,-46.6345,-1.6) rot=(0.707107,0.707107,0;3.14159rad)
FEATURE [App::Link] C37_C_0603_1608Metric_611CB56A_ln_001  label="C35_C_0603_1608Metric_611CB556"
  LinkPlacement = pos=(-42.989,-46.2285,-1.6) rot=(0.707107,0.707107,0;3.14159rad)
  LinkedObject = -> Shape003
  Placement = pos=(-42.989,-46.2285,-1.6) rot=(0.707107,0.707107,0;3.14159rad)
FEATURE [App::Link] C37_C_0603_1608Metric_611CB56A_ln_002  label="C34_C_0603_1608Metric_611CB54C"
  LinkPlacement = pos=(-100.108,-46.3235,-1.6) rot=(0.707107,0.707107,0;3.14159rad)
  LinkedObject = -> Shape003
  Placement = pos=(-100.108,-46.3235,-1.6) rot=(0.707107,0.707107,0;3.14159rad)
FEATURE [App::Link] C37_C_0603_1608Metric_611CB56A_ln_003  label="C33_C_0603_1608Metric_611CB542"
  LinkPlacement = pos=(-118.618,-34.3535,-1.6) rot=(1,0,0;3.14159rad)
  LinkedObject = -> Shape003
  Placement = pos=(-118.618,-34.3535,-1.6) rot=(1,0,0;3.14159rad)
FEATURE [App::Link] C37_C_0603_1608Metric_611CB56A_ln_004  label="C32_C_0603_1608Metric_611CB538"
  LinkPlacement = pos=(-61.595,-34.3535,-1.6) rot=(1,0,0;3.14159rad)
  LinkedObject = -> Shape003
  Placement = pos=(-61.595,-34.3535,-1.6) rot=(1,0,0;3.14159rad)
FEATURE [App::Link] C37_C_0603_1608Metric_611CB56A_ln_005  label="C31_C_0603_1608Metric_611CB52E"
  LinkPlacement = pos=(4.953,-34.3535,-1.6) rot=(1,0,0;3.14159rad)
  LinkedObject = -> Shape003
  Placement = pos=(4.953,-34.3535,-1.6) rot=(1,0,0;3.14159rad)
FEATURE [App::Link] C37_C_0603_1608Metric_611CB56A_ln_006  label="C30_C_0603_1608Metric_611CB524"
  LinkPlacement = pos=(71.704,-34.3785,-1.6) rot=(1,0,0;3.14159rad)
  LinkedObject = -> Shape003
  Placement = pos=(71.704,-34.3785,-1.6) rot=(1,0,0;3.14159rad)
FEATURE [App::Link] C37_C_0603_1608Metric_611CB56A_ln_007  label="C29_C_0603_1608Metric_611CB51A"
  LinkPlacement = pos=(129.032,-34.3535,-1.6) rot=(1,0,0;3.14159rad)
  LinkedObject = -> Shape003
  Placement = pos=(129.032,-34.3535,-1.6) rot=(1,0,0;3.14159rad)
FEATURE [App::Link] C37_C_0603_1608Metric_611CB56A_ln_008  label="C28_C_0603_1608Metric_611CB510"
  LinkPlacement = pos=(128.905,-15.3035,-1.6) rot=(1,0,0;3.14159rad)
  LinkedObject = -> Shape003
  Placement = pos=(128.905,-15.3035,-1.6) rot=(1,0,0;3.14159rad)
FEATURE [App::Link] C37_C_0603_1608Metric_611CB56A_ln_009  label="C27_C_0603_1608Metric_611CB506"
  LinkPlacement = pos=(71.882,-15.3035,-1.6) rot=(1,0,0;3.14159rad)
  LinkedObject = -> Shape003
  Placement = pos=(71.882,-15.3035,-1.6) rot=(1,0,0;3.14159rad)
FEATURE [App::Link] C37_C_0603_1608Metric_611CB56A_ln_010  label="C26_C_0603_1608Metric_611CB4FC"
  LinkPlacement = pos=(4.953,-15.3035,-1.6) rot=(1,0,0;3.14159rad)
  LinkedObject = -> Shape003
  Placement = pos=(4.953,-15.3035,-1.6) rot=(1,0,0;3.14159rad)
FEATURE [App::Link] C37_C_0603_1608Metric_611CB56A_ln_011  label="C25_C_0603_1608Metric_611CB4F2"
  LinkPlacement = pos=(-61.595,-15.3035,-1.6) rot=(1,0,0;3.14159rad)
  LinkedObject = -> Shape003
  Placement = pos=(-61.595,-15.3035,-1.6) rot=(1,0,0;3.14159rad)
FEATURE [App::Link] C37_C_0603_1608Metric_611CB56A_ln_012  label="C24_C_0603_1608Metric_611CB4E8"
  LinkPlacement = pos=(-118.745,-15.3035,-1.6) rot=(1,0,0;3.14159rad)
  LinkedObject = -> Shape003
  Placement = pos=(-118.745,-15.3035,-1.6) rot=(1,0,0;3.14159rad)
FEATURE [App::Link] C37_C_0603_1608Metric_611CB56A_ln_013  label="C23_C_0603_1608Metric_611CB4DE"
  LinkPlacement = pos=(-118.745,3.7465,-1.6) rot=(1,0,0;3.14159rad)
  LinkedObject = -> Shape003
  Placement = pos=(-118.745,3.7465,-1.6) rot=(1,0,0;3.14159rad)
FEATURE [App::Link] C37_C_0603_1608Metric_611CB56A_ln_014  label="C22_C_0603_1608Metric_611CB4D4"
  LinkPlacement = pos=(-61.595,3.7465,-1.6) rot=(1,0,0;3.14159rad)
  LinkedObject = -> Shape003
  Placement = pos=(-61.595,3.7465,-1.6) rot=(1,0,0;3.14159rad)
FEATURE [App::Link] C37_C_0603_1608Metric_611CB56A_ln_015  label="C21_C_0603_1608Metric_611CB4CA"
  LinkPlacement = pos=(4.953,3.7465,-1.6) rot=(1,0,0;3.14159rad)
  LinkedObject = -> Shape003
  Placement = pos=(4.953,3.7465,-1.6) rot=(1,0,0;3.14159rad)
FEATURE [App::Link] C37_C_0603_1608Metric_611CB56A_ln_016  label="C20_C_0603_1608Metric_611CB4C0"
  LinkPlacement = pos=(71.755,3.7465,-1.6) rot=(1,0,0;3.14159rad)
  LinkedObject = -> Shape003
  Placement = pos=(71.755,3.7465,-1.6) rot=(1,0,0;3.14159rad)
FEATURE [App::Link] C37_C_0603_1608Metric_611CB56A_ln_017  label="C19_C_0603_1608Metric_611CB4B6"
  LinkPlacement = pos=(128.778,3.7465,-1.6) rot=(1,0,0;3.14159rad)
  LinkedObject = -> Shape003
  Placement = pos=(128.778,3.7465,-1.6) rot=(1,0,0;3.14159rad)
FEATURE [App::Link] C37_C_0603_1608Metric_611CB56A_ln_018  label="C18_C_0603_1608Metric_611CB4AC"
  LinkPlacement = pos=(128.905,22.7965,-1.6) rot=(1,0,0;3.14159rad)
  LinkedObject = -> Shape003
  Placement = pos=(128.905,22.7965,-1.6) rot=(1,0,0;3.14159rad)
FEATURE [App::Link] C37_C_0603_1608Metric_611CB56A_ln_019  label="C17_C_0603_1608Metric_611CB4A2"
  LinkPlacement = pos=(71.628,22.7965,-1.6) rot=(1,0,0;3.14159rad)
  LinkedObject = -> Shape003
  Placement = pos=(71.628,22.7965,-1.6) rot=(1,0,0;3.14159rad)
FEATURE [App::Link] C37_C_0603_1608Metric_611CB56A_ln_020  label="C16_C_0603_1608Metric_611CB498"
  LinkPlacement = pos=(4.953,22.7965,-1.6) rot=(1,0,0;3.14159rad)
  LinkedObject = -> Shape003
  Placement = pos=(4.953,22.7965,-1.6) rot=(1,0,0;3.14159rad)
FEATURE [App::Link] C37_C_0603_1608Metric_611CB56A_ln_021  label="C15_C_0603_1608Metric_611CB48E"
  LinkPlacement = pos=(-61.722,22.7965,-1.6) rot=(1,0,0;3.14159rad)
  LinkedObject = -> Shape003
  Placement = pos=(-61.722,22.7965,-1.6) rot=(1,0,0;3.14159rad)
FEATURE [App::Link] C37_C_0603_1608Metric_611CB56A_ln_022  label="C14_C_0603_1608Metric_611CB484"
  LinkPlacement = pos=(-118.745,22.9235,-1.6) rot=(1,0,0;3.14159rad)
  LinkedObject = -> Shape003
  Placement = pos=(-118.745,22.9235,-1.6) rot=(1,0,0;3.14159rad)
FEATURE [App::Link] C37_C_0603_1608Metric_611CB56A_ln_023  label="C13_C_0603_1608Metric_611CB47A"
  LinkPlacement = pos=(-145.962,22.8283,-1.6) rot=(0,1,0;3.14159rad)
  LinkedObject = -> Shape003
  Placement = pos=(-145.962,22.8283,-1.6) rot=(0,1,0;3.14159rad)
FEATURE [App::Link] C37_C_0603_1608Metric_611CB56A_ln_024  label="C12_C_0603_1608Metric_611CB470"
  LinkPlacement = pos=(-140.716,26.7335,-1.6) rot=(-0.707107,0.707107,0;3.14159rad)
  LinkedObject = -> Shape003
  Placement = pos=(-140.716,26.7335,-1.6) rot=(-0.707107,0.707107,0;3.14159rad)
FEATURE [App::Link] C37_C_0603_1608Metric_611CB56A_ln_025  label="C11_C_0603_1608Metric_611CB466"
  LinkPlacement = pos=(-31.623,4.6355,-1.6) rot=(1,0,0;3.14159rad)
  LinkedObject = -> Shape003
  Placement = pos=(-31.623,4.6355,-1.6) rot=(1,0,0;3.14159rad)
FEATURE [App::Link] C37_C_0603_1608Metric_611CB56A_ln_026  label="C10_C_0603_1608Metric_611CB45C"
  LinkPlacement = pos=(-30.734,-1.2065,-1.6) rot=(1,0,0;3.14159rad)
  LinkedObject = -> Shape003
  Placement = pos=(-30.734,-1.2065,-1.6) rot=(1,0,0;3.14159rad)
FEATURE [App::Link] C37_C_0603_1608Metric_611CB56A_ln_027  label="C9_C_0603_1608Metric_611CB452"
  LinkPlacement = pos=(-79.375,19.05,-1.6) rot=(-0.707107,0.707107,0;3.14159rad)
  LinkedObject = -> Shape003
  Placement = pos=(-79.375,19.05,-1.6) rot=(-0.707107,0.707107,0;3.14159rad)
FEATURE [App::Link] C37_C_0603_1608Metric_611CB56A_ln_028  label="C8_C_0603_1608Metric_611CB448"
  LinkPlacement = pos=(-85.725,19.05,-1.6) rot=(-0.707107,0.707107,0;3.14159rad)
  LinkedObject = -> Shape003
  Placement = pos=(-85.725,19.05,-1.6) rot=(-0.707107,0.707107,0;3.14159rad)
FEATURE [App::Link] C37_C_0603_1608Metric_611CB56A_ln_029  label="C7_C_0603_1608Metric_611CB43E"
  LinkPlacement = pos=(-154.464,33.6233,-1.6) rot=(-0.707107,0.707107,0;3.14159rad)
  LinkedObject = -> Shape003
  Placement = pos=(-154.464,33.6233,-1.6) rot=(-0.707107,0.707107,0;3.14159rad)
FEATURE [App::Link] C37_C_0603_1608Metric_611CB56A_ln_030  label="C6_C_0603_1608Metric_611CB434"
  LinkPlacement = pos=(-42.926,-8.1915,-1.6) rot=(0.707107,0.707107,0;3.14159rad)
  LinkedObject = -> Shape003
  Placement = pos=(-42.926,-8.1915,-1.6) rot=(0.707107,0.707107,0;3.14159rad)
FEATURE [App::Link] C37_C_0603_1608Metric_611CB56A_ln_031  label="C5_C_0603_1608Metric_611CB42A"
  LinkPlacement = pos=(-36.449,-3.7465,-1.6) rot=(0.707107,0.707107,0;3.14159rad)
  LinkedObject = -> Shape003
  Placement = pos=(-36.449,-3.7465,-1.6) rot=(0.707107,0.707107,0;3.14159rad)
FEATURE [App::Link] C37_C_0603_1608Metric_611CB56A_ln_032  label="C4_C_0603_1608Metric_611CB420"
  LinkPlacement = pos=(-46.101,-8.1915,-1.6) rot=(0.707107,0.707107,0;3.14159rad)
  LinkedObject = -> Shape003
  Placement = pos=(-46.101,-8.1915,-1.6) rot=(0.707107,0.707107,0;3.14159rad)
FEATURE [App::Link] C37_C_0603_1608Metric_611CB56A_ln_033  label="C3_C_0603_1608Metric_611CB416"
  LinkPlacement = pos=(-53.848,4.8895,-1.6) rot=(1,0,0;3.14159rad)
  LinkedObject = -> Shape003
  Placement = pos=(-53.848,4.8895,-1.6) rot=(1,0,0;3.14159rad)
FEATURE [App::Link] C37_C_0603_1608Metric_611CB56A_ln_034  label="C2_C_0603_1608Metric_611CB40C"
  LinkPlacement = pos=(-42.799,10.7315,-1.6) rot=(-0.707107,0.707107,0;3.14159rad)
  LinkedObject = -> Shape003
  Placement = pos=(-42.799,10.7315,-1.6) rot=(-0.707107,0.707107,0;3.14159rad)
FEATURE [App::Link] C37_C_0603_1608Metric_611CB56A_ln_035  label="C1_C_0603_1608Metric_611CB402"
  LinkPlacement = pos=(-56.388,4.0005,-1.6) rot=(-0.707107,0.707107,0;3.14159rad)
  LinkedObject = -> Shape003
  Placement = pos=(-56.388,4.0005,-1.6) rot=(-0.707107,0.707107,0;3.14159rad)
FEATURE [Part::Feature] Shape004  label="D_2_D_SOD_123_611CB7E4"
  Placement = pos=(-122.047,47.371,-1.6) rot=(0.707107,0.707107,0;3.14159rad)
  shape: bbox 1.6 x 3.8 x 1.25 mm, 67 faces (baked)
FEATURE [App::Link] D_2_D_SOD_123_611CB7E4_ln_  label="D_1_2_D_SOD_123_611CB7D3"
  LinkPlacement = pos=(-141.224,47.371,-1.6) rot=(0.707107,0.707107,0;3.14159rad)
  LinkedObject = -> Shape004
  Placement = pos=(-141.224,47.371,-1.6) rot=(0.707107,0.707107,0;3.14159rad)
FEATURE [App::Link] D_2_D_SOD_123_611CB7E4_ln_001  label="D_100_2_D_SOD_123_611CBE66"
  LinkPlacement = pos=(147.637,-47.2435,-1.6) rot=(0.707107,0.707107,0;3.14159rad)
  LinkedObject = -> Shape004
  Placement = pos=(147.637,-47.2435,-1.6) rot=(0.707107,0.707107,0;3.14159rad)
FEATURE [App::Link] D_2_D_SOD_123_611CB7E4_ln_002  label="D_99_2_D_SOD_123_611CBE55"
  LinkPlacement = pos=(144.526,-47.2435,-1.6) rot=(0.707107,0.707107,0;3.14159rad)
  LinkedObject = -> Shape004
  Placement = pos=(144.526,-47.2435,-1.6) rot=(0.707107,0.707107,0;3.14159rad)
FEATURE [App::Link] D_2_D_SOD_123_611CB7E4_ln_003  label="D_98_2_D_SOD_123_611CBE44"
  LinkPlacement = pos=(125.667,-47.2435,-1.6) rot=(0.707107,0.707107,0;3.14159rad)
  LinkedObject = -> Shape004
  Placement = pos=(125.667,-47.2435,-1.6) rot=(0.707107,0.707107,0;3.14159rad)
FEATURE [App::Link] D_2_D_SOD_123_611CB7E4_ln_004  label="D_97_2_D_SOD_123_611CBE33"
  LinkPlacement = pos=(106.363,-47.2435,-1.6) rot=(0.707107,0.707107,0;3.14159rad)
  LinkedObject = -> Shape004
  Placement = pos=(106.363,-47.2435,-1.6) rot=(0.707107,0.707107,0;3.14159rad)
FEATURE [App::Link] D_2_D_SOD_123_611CB7E4_ln_005  label="D_96_2_D_SOD_123_611CBE22"
  LinkPlacement = pos=(87.313,-47.2435,-1.6) rot=(0.707107,0.707107,0;3.14159rad)
  LinkedObject = -> Shape004
  Placement = pos=(87.313,-47.2435,-1.6) rot=(0.707107,0.707107,0;3.14159rad)
FEATURE [App::Link] D_2_D_SOD_123_611CB7E4_ln_006  label="D_95_2_D_SOD_123_611CBE11"
  LinkPlacement = pos=(68.263,-47.2435,-1.6) rot=(0.707107,0.707107,0;3.14159rad)
  LinkedObject = -> Shape004
  Placement = pos=(68.263,-47.2435,-1.6) rot=(0.707107,0.707107,0;3.14159rad)
FEATURE [App::Link] D_2_D_SOD_123_611CB7E4_ln_007  label="D_94_2_D_SOD_123_611CBE00"
  LinkPlacement = pos=(49.213,-47.2435,-1.6) rot=(0.707107,0.707107,0;3.14159rad)
  LinkedObject = -> Shape004
  Placement = pos=(49.213,-47.2435,-1.6) rot=(0.707107,0.707107,0;3.14159rad)
FEATURE [App::Link] D_2_D_SOD_123_611CB7E4_ln_008  label="D_93_2_D_SOD_123_611CBDEF"
  LinkPlacement = pos=(30.163,-47.2435,-1.6) rot=(0.707107,0.707107,0;3.14159rad)
  LinkedObject = -> Shape004
  Placement = pos=(30.163,-47.2435,-1.6) rot=(0.707107,0.707107,0;3.14159rad)
FEATURE [App::Link] D_2_D_SOD_123_611CB7E4_ln_009  label="D_92_2_D_SOD_123_611CBDDE"
  LinkPlacement = pos=(11.113,-47.2435,-1.6) rot=(0.707107,0.707107,0;3.14159rad)
  LinkedObject = -> Shape004
  Placement = pos=(11.113,-47.2435,-1.6) rot=(0.707107,0.707107,0;3.14159rad)
FEATURE [App::Link] D_2_D_SOD_123_611CB7E4_ln_010  label="D_91_2_D_SOD_123_611CBDCD"
  LinkPlacement = pos=(-7.937,-47.2435,-1.6) rot=(0.707107,0.707107,0;3.14159rad)
  LinkedObject = -> Shape004
  Placement = pos=(-7.937,-47.2435,-1.6) rot=(0.707107,0.707107,0;3.14159rad)
FEATURE [App::Link] D_2_D_SOD_123_611CB7E4_ln_011  label="D_90_2_D_SOD_123_611CBDBC"
  LinkPlacement = pos=(-26.987,-47.2435,-1.6) rot=(0.707107,0.707107,0;3.14159rad)
  LinkedObject = -> Shape004
  Placement = pos=(-26.987,-47.2435,-1.6) rot=(0.707107,0.707107,0;3.14159rad)
FEATURE [App::Link] D_2_D_SOD_123_611CB7E4_ln_012  label="D_89_2_D_SOD_123_611CBDAB"
  LinkPlacement = pos=(-45.974,-47.2435,-1.6) rot=(0.707107,0.707107,0;3.14159rad)
  LinkedObject = -> Shape004
  Placement = pos=(-45.974,-47.2435,-1.6) rot=(0.707107,0.707107,0;3.14159rad)
FEATURE [App::Link] D_2_D_SOD_123_611CB7E4_ln_013  label="D_88_2_D_SOD_123_611CBD9A"
  LinkPlacement = pos=(-65.024,-47.2435,-1.6) rot=(0.707107,0.707107,0;3.14159rad)
  LinkedObject = -> Shape004
  Placement = pos=(-65.024,-47.2435,-1.6) rot=(0.707107,0.707107,0;3.14159rad)
FEATURE [App::Link] D_2_D_SOD_123_611CB7E4_ln_014  label="D_87_2_D_SOD_123_611CBD89"
  LinkPlacement = pos=(-84.1375,-47.2435,-1.6) rot=(0.707107,0.707107,0;3.14159rad)
  LinkedObject = -> Shape004
  Placement = pos=(-84.1375,-47.2435,-1.6) rot=(0.707107,0.707107,0;3.14159rad)
FEATURE [App::Link] D_2_D_SOD_123_611CB7E4_ln_015  label="D_86_2_D_SOD_123_611CBD78"
  LinkPlacement = pos=(-103.124,-47.2435,-1.6) rot=(0.707107,0.707107,0;3.14159rad)
  LinkedObject = -> Shape004
  Placement = pos=(-103.124,-47.2435,-1.6) rot=(0.707107,0.707107,0;3.14159rad)
FEATURE [App::Link] D_2_D_SOD_123_611CB7E4_ln_016  label="D_85_2_D_SOD_123_611CBD67"
  LinkPlacement = pos=(-122.047,-47.2435,-1.6) rot=(0.707107,0.707107,0;3.14159rad)
  LinkedObject = -> Shape004
  Placement = pos=(-122.047,-47.2435,-1.6) rot=(0.707107,0.707107,0;3.14159rad)
FEATURE [App::Link] D_2_D_SOD_123_611CB7E4_ln_017  label="D_84_2_D_SOD_123_611CBD56"
  LinkPlacement = pos=(-141.224,-47.2435,-1.6) rot=(0.707107,0.707107,0;3.14159rad)
  LinkedObject = -> Shape004
  Placement = pos=(-141.224,-47.2435,-1.6) rot=(0.707107,0.707107,0;3.14159rad)
FEATURE [App::Link] D_2_D_SOD_123_611CB7E4_ln_018  label="D_83_2_D_SOD_123_611CBD45"
  LinkPlacement = pos=(144.526,-21.4635,-1.6) rot=(0.707107,0.707107,0;3.14159rad)
  LinkedObject = -> Shape004
  Placement = pos=(144.526,-21.4635,-1.6) rot=(0.707107,0.707107,0;3.14159rad)
FEATURE [App::Link] D_2_D_SOD_123_611CB7E4_ln_019  label="D_82_2_D_SOD_123_611CBD34"
  LinkPlacement = pos=(128.587,-28.2575,-1.6) rot=(0.707107,0.707107,0;3.14159rad)
  LinkedObject = -> Shape004
  Placement = pos=(128.587,-28.2575,-1.6) rot=(0.707107,0.707107,0;3.14159rad)
FEATURE [App::Link] D_2_D_SOD_123_611CB7E4_ln_020  label="D_81_2_D_SOD_123_611CBD23"
  LinkPlacement = pos=(125.667,-28.2575,-1.6) rot=(0.707107,0.707107,0;3.14159rad)
  LinkedObject = -> Shape004
  Placement = pos=(125.667,-28.2575,-1.6) rot=(0.707107,0.707107,0;3.14159rad)
FEATURE [App::Link] D_2_D_SOD_123_611CB7E4_ln_021  label="D_80_2_D_SOD_123_611CBD12"
  LinkPlacement = pos=(106.363,-28.1935,-1.6) rot=(0.707107,0.707107,0;3.14159rad)
  LinkedObject = -> Shape004
  Placement = pos=(106.363,-28.1935,-1.6) rot=(0.707107,0.707107,0;3.14159rad)
FEATURE [App::Link] D_2_D_SOD_123_611CB7E4_ln_022  label="D_79_2_D_SOD_123_611CBD01"
  LinkPlacement = pos=(87.313,-28.1935,-1.6) rot=(0.707107,0.707107,0;3.14159rad)
  LinkedObject = -> Shape004
  Placement = pos=(87.313,-28.1935,-1.6) rot=(0.707107,0.707107,0;3.14159rad)
FEATURE [App::Link] D_2_D_SOD_123_611CB7E4_ln_023  label="D_78_2_D_SOD_123_611CBCF0"
  LinkPlacement = pos=(68.263,-28.1935,-1.6) rot=(0.707107,0.707107,0;3.14159rad)
  LinkedObject = -> Shape004
  Placement = pos=(68.263,-28.1935,-1.6) rot=(0.707107,0.707107,0;3.14159rad)
FEATURE [App::Link] D_2_D_SOD_123_611CB7E4_ln_024  label="D_77_2_D_SOD_123_611CBCDF"
  LinkPlacement = pos=(49.213,-28.1935,-1.6) rot=(0.707107,0.707107,0;3.14159rad)
  LinkedObject = -> Shape004
  Placement = pos=(49.213,-28.1935,-1.6) rot=(0.707107,0.707107,0;3.14159rad)
FEATURE [App::Link] D_2_D_SOD_123_611CB7E4_ln_025  label="D_76_2_D_SOD_123_611CBCCE"
  LinkPlacement = pos=(30.163,-28.1935,-1.6) rot=(0.707107,0.707107,0;3.14159rad)
  LinkedObject = -> Shape004
  Placement = pos=(30.163,-28.1935,-1.6) rot=(0.707107,0.707107,0;3.14159rad)
FEATURE [App::Link] D_2_D_SOD_123_611CB7E4_ln_026  label="D_75_2_D_SOD_123_611CBCBD"
  LinkPlacement = pos=(11.113,-28.1935,-1.6) rot=(0.707107,0.707107,0;3.14159rad)
  LinkedObject = -> Shape004
  Placement = pos=(11.113,-28.1935,-1.6) rot=(0.707107,0.707107,0;3.14159rad)
FEATURE [App::Link] D_2_D_SOD_123_611CB7E4_ln_027  label="D_74_2_D_SOD_123_611CBCAC"
  LinkPlacement = pos=(-7.937,-28.1935,-1.6) rot=(0.707107,0.707107,0;3.14159rad)
  LinkedObject = -> Shape004
  Placement = pos=(-7.937,-28.1935,-1.6) rot=(0.707107,0.707107,0;3.14159rad)
FEATURE [App::Link] D_2_D_SOD_123_611CB7E4_ln_028  label="D_73_2_D_SOD_123_611CBC9B"
  LinkPlacement = pos=(-26.987,-28.1935,-1.6) rot=(0.707107,0.707107,0;3.14159rad)
  LinkedObject = -> Shape004
  Placement = pos=(-26.987,-28.1935,-1.6) rot=(0.707107,0.707107,0;3.14159rad)
FEATURE [App::Link] D_2_D_SOD_123_611CB7E4_ln_029  label="D_72_2_D_SOD_123_611CBC8A"
  LinkPlacement = pos=(-45.974,-28.1935,-1.6) rot=(0.707107,0.707107,0;3.14159rad)
  LinkedObject = -> Shape004
  Placement = pos=(-45.974,-28.1935,-1.6) rot=(0.707107,0.707107,0;3.14159rad)
FEATURE [App::Link] D_2_D_SOD_123_611CB7E4_ln_030  label="D_71_2_D_SOD_123_611CBC79"
  LinkPlacement = pos=(-65.024,-28.1935,-1.6) rot=(0.707107,0.707107,0;3.14159rad)
  LinkedObject = -> Shape004
  Placement = pos=(-65.024,-28.1935,-1.6) rot=(0.707107,0.707107,0;3.14159rad)
FEATURE [App::Link] D_2_D_SOD_123_611CB7E4_ln_031  label="D_70_2_D_SOD_123_611CBC68"
  LinkPlacement = pos=(-84.1375,-28.1935,-1.6) rot=(0.707107,0.707107,0;3.14159rad)
  LinkedObject = -> Shape004
  Placement = pos=(-84.1375,-28.1935,-1.6) rot=(0.707107,0.707107,0;3.14159rad)
FEATURE [App::Link] D_2_D_SOD_123_611CB7E4_ln_032  label="D_69_2_D_SOD_123_611CBC57"
  LinkPlacement = pos=(-103.124,-28.1935,-1.6) rot=(0.707107,0.707107,0;3.14159rad)
  LinkedObject = -> Shape004
  Placement = pos=(-103.124,-28.1935,-1.6) rot=(0.707107,0.707107,0;3.14159rad)
FEATURE [App::Link] D_2_D_SOD_123_611CB7E4_ln_033  label="D_68_2_D_SOD_123_611CBC46"
  LinkPlacement = pos=(-122.047,-28.0035,-1.6) rot=(0.707107,0.707107,0;3.14159rad)
  LinkedObject = -> Shape004
  Placement = pos=(-122.047,-28.0035,-1.6) rot=(0.707107,0.707107,0;3.14159rad)
FEATURE [App::Link] D_2_D_SOD_123_611CB7E4_ln_034  label="D_67_2_D_SOD_123_611CBC35"
  LinkPlacement = pos=(-141.224,-34.6075,-1.6) rot=(0.707107,0.707107,0;3.14159rad)
  LinkedObject = -> Shape004
  Placement = pos=(-141.224,-34.6075,-1.6) rot=(0.707107,0.707107,0;3.14159rad)
FEATURE [App::Link] D_2_D_SOD_123_611CB7E4_ln_035  label="D_66_2_D_SOD_123_611CBC24"
  LinkPlacement = pos=(144.526,-2.3495,-1.6) rot=(0.707107,0.707107,0;3.14159rad)
  LinkedObject = -> Shape004
  Placement = pos=(144.526,-2.3495,-1.6) rot=(0.707107,0.707107,0;3.14159rad)
FEATURE [App::Link] D_2_D_SOD_123_611CB7E4_ln_036  label="D_65_2_D_SOD_123_611CBC13"
  LinkPlacement = pos=(128.587,-9.144,-1.6) rot=(0.707107,0.707107,0;3.14159rad)
  LinkedObject = -> Shape004
  Placement = pos=(128.587,-9.144,-1.6) rot=(0.707107,0.707107,0;3.14159rad)
FEATURE [App::Link] D_2_D_SOD_123_611CB7E4_ln_037  label="D_64_2_D_SOD_123_611CBC02"
  LinkPlacement = pos=(125.667,-9.144,-1.6) rot=(0.707107,0.707107,0;3.14159rad)
  LinkedObject = -> Shape004
  Placement = pos=(125.667,-9.144,-1.6) rot=(0.707107,0.707107,0;3.14159rad)
FEATURE [App::Link] D_2_D_SOD_123_611CB7E4_ln_038  label="D_63_2_D_SOD_123_611CBBF1"
  LinkPlacement = pos=(106.363,-9.144,-1.6) rot=(0.707107,0.707107,0;3.14159rad)
  LinkedObject = -> Shape004
  Placement = pos=(106.363,-9.144,-1.6) rot=(0.707107,0.707107,0;3.14159rad)
FEATURE [App::Link] D_2_D_SOD_123_611CB7E4_ln_039  label="D_62_2_D_SOD_123_611CBBE0"
  LinkPlacement = pos=(87.313,-9.144,-1.6) rot=(0.707107,0.707107,0;3.14159rad)
  LinkedObject = -> Shape004
  Placement = pos=(87.313,-9.144,-1.6) rot=(0.707107,0.707107,0;3.14159rad)
FEATURE [App::Link] D_2_D_SOD_123_611CB7E4_ln_040  label="D_61_2_D_SOD_123_611CBBCF"
  LinkPlacement = pos=(68.263,-9.144,-1.6) rot=(0.707107,0.707107,0;3.14159rad)
  LinkedObject = -> Shape004
  Placement = pos=(68.263,-9.144,-1.6) rot=(0.707107,0.707107,0;3.14159rad)
FEATURE [App::Link] D_2_D_SOD_123_611CB7E4_ln_041  label="D_60_2_D_SOD_123_611CBBBE"
  LinkPlacement = pos=(49.213,-9.144,-1.6) rot=(0.707107,0.707107,0;3.14159rad)
  LinkedObject = -> Shape004
  Placement = pos=(49.213,-9.144,-1.6) rot=(0.707107,0.707107,0;3.14159rad)
FEATURE [App::Link] D_2_D_SOD_123_611CB7E4_ln_042  label="D_59_2_D_SOD_123_611CBBAD"
  LinkPlacement = pos=(30.163,-9.144,-1.6) rot=(0.707107,0.707107,0;3.14159rad)
  LinkedObject = -> Shape004
  Placement = pos=(30.163,-9.144,-1.6) rot=(0.707107,0.707107,0;3.14159rad)
FEATURE [App::Link] D_2_D_SOD_123_611CB7E4_ln_043  label="D_58_2_D_SOD_123_611CBB9C"
  LinkPlacement = pos=(11.113,-9.144,-1.6) rot=(0.707107,0.707107,0;3.14159rad)
  LinkedObject = -> Shape004
  Placement = pos=(11.113,-9.144,-1.6) rot=(0.707107,0.707107,0;3.14159rad)
FEATURE [App::Link] D_2_D_SOD_123_611CB7E4_ln_044  label="D_57_2_D_SOD_123_611CBB8B"
  LinkPlacement = pos=(-7.937,-9.144,-1.6) rot=(0.707107,0.707107,0;3.14159rad)
  LinkedObject = -> Shape004
  Placement = pos=(-7.937,-9.144,-1.6) rot=(0.707107,0.707107,0;3.14159rad)
FEATURE [App::Link] D_2_D_SOD_123_611CB7E4_ln_045  label="D_56_2_D_SOD_123_611CBB7A"
  LinkPlacement = pos=(-26.987,-9.144,-1.6) rot=(0.707107,0.707107,0;3.14159rad)
  LinkedObject = -> Shape004
  Placement = pos=(-26.987,-9.144,-1.6) rot=(0.707107,0.707107,0;3.14159rad)
FEATURE [App::Link] D_2_D_SOD_123_611CB7E4_ln_046  label="D_55_2_D_SOD_123_611CBB69"
  LinkPlacement = pos=(-61.976,-9.144,-1.6) rot=(0.707107,0.707107,0;3.14159rad)
  LinkedObject = -> Shape004
  Placement = pos=(-61.976,-9.144,-1.6) rot=(0.707107,0.707107,0;3.14159rad)
FEATURE [App::Link] D_2_D_SOD_123_611CB7E4_ln_047  label="D_54_2_D_SOD_123_611CBB58"
  LinkPlacement = pos=(-65.024,-9.144,-1.6) rot=(0.707107,0.707107,0;3.14159rad)
  LinkedObject = -> Shape004
  Placement = pos=(-65.024,-9.144,-1.6) rot=(0.707107,0.707107,0;3.14159rad)
FEATURE [App::Link] D_2_D_SOD_123_611CB7E4_ln_048  label="D_53_2_D_SOD_123_611CBB47"
  LinkPlacement = pos=(-84.1375,-9.144,-1.6) rot=(0.707107,0.707107,0;3.14159rad)
  LinkedObject = -> Shape004
  Placement = pos=(-84.1375,-9.144,-1.6) rot=(0.707107,0.707107,0;3.14159rad)
FEATURE [App::Link] D_2_D_SOD_123_611CB7E4_ln_049  label="D_52_2_D_SOD_123_611CBB36"
  LinkPlacement = pos=(-103.124,-9.144,-1.6) rot=(0.707107,0.707107,0;3.14159rad)
  LinkedObject = -> Shape004
  Placement = pos=(-103.124,-9.144,-1.6) rot=(0.707107,0.707107,0;3.14159rad)
FEATURE [App::Link] D_2_D_SOD_123_611CB7E4_ln_050  label="D_51_2_D_SOD_123_611CBB25"
  LinkPlacement = pos=(-122.047,-9.144,-1.6) rot=(0.707107,0.707107,0;3.14159rad)
  LinkedObject = -> Shape004
  Placement = pos=(-122.047,-9.144,-1.6) rot=(0.707107,0.707107,0;3.14159rad)
FEATURE [App::Link] D_2_D_SOD_123_611CB7E4_ln_051  label="D_50_2_D_SOD_123_611CBB14"
  LinkPlacement = pos=(-141.224,-15.4305,-1.6) rot=(0.707107,0.707107,0;3.14159rad)
  LinkedObject = -> Shape004
  Placement = pos=(-141.224,-15.4305,-1.6) rot=(0.707107,0.707107,0;3.14159rad)
FEATURE [App::Link] D_2_D_SOD_123_611CB7E4_ln_052  label="D_49_2_D_SOD_123_611CBB03"
  LinkPlacement = pos=(147.637,9.9695,-1.6) rot=(0.707107,0.707107,0;3.14159rad)
  LinkedObject = -> Shape004
  Placement = pos=(147.637,9.9695,-1.6) rot=(0.707107,0.707107,0;3.14159rad)
FEATURE [App::Link] D_2_D_SOD_123_611CB7E4_ln_053  label="D_48_2_D_SOD_123_611CBAF2"
  LinkPlacement = pos=(144.526,9.9695,-1.6) rot=(0.707107,0.707107,0;3.14159rad)
  LinkedObject = -> Shape004
  Placement = pos=(144.526,9.9695,-1.6) rot=(0.707107,0.707107,0;3.14159rad)
FEATURE [App::Link] D_2_D_SOD_123_611CB7E4_ln_054  label="D_47_2_D_SOD_123_611CBAE1"
  LinkPlacement = pos=(125.667,9.9695,-1.6) rot=(0.707107,0.707107,0;3.14159rad)
  LinkedObject = -> Shape004
  Placement = pos=(125.667,9.9695,-1.6) rot=(0.707107,0.707107,0;3.14159rad)
FEATURE [App::Link] D_2_D_SOD_123_611CB7E4_ln_055  label="D_46_2_D_SOD_123_611CBAD0"
  LinkPlacement = pos=(106.363,9.9695,-1.6) rot=(0.707107,0.707107,0;3.14159rad)
  LinkedObject = -> Shape004
  Placement = pos=(106.363,9.9695,-1.6) rot=(0.707107,0.707107,0;3.14159rad)
FEATURE [App::Link] D_2_D_SOD_123_611CB7E4_ln_056  label="D_45_2_D_SOD_123_611CBABF"
  LinkPlacement = pos=(87.313,9.9695,-1.6) rot=(0.707107,0.707107,0;3.14159rad)
  LinkedObject = -> Shape004
  Placement = pos=(87.313,9.9695,-1.6) rot=(0.707107,0.707107,0;3.14159rad)
FEATURE [App::Link] D_2_D_SOD_123_611CB7E4_ln_057  label="D_44_2_D_SOD_123_611CBAAE"
  LinkPlacement = pos=(68.263,9.9695,-1.6) rot=(0.707107,0.707107,0;3.14159rad)
  LinkedObject = -> Shape004
  Placement = pos=(68.263,9.9695,-1.6) rot=(0.707107,0.707107,0;3.14159rad)
FEATURE [App::Link] D_2_D_SOD_123_611CB7E4_ln_058  label="D_43_2_D_SOD_123_611CBA9D"
  LinkPlacement = pos=(49.213,9.9695,-1.6) rot=(0.707107,0.707107,0;3.14159rad)
  LinkedObject = -> Shape004
  Placement = pos=(49.213,9.9695,-1.6) rot=(0.707107,0.707107,0;3.14159rad)
FEATURE [App::Link] D_2_D_SOD_123_611CB7E4_ln_059  label="D_42_2_D_SOD_123_611CBA8C"
  LinkPlacement = pos=(30.163,9.9695,-1.6) rot=(0.707107,0.707107,0;3.14159rad)
  LinkedObject = -> Shape004
  Placement = pos=(30.163,9.9695,-1.6) rot=(0.707107,0.707107,0;3.14159rad)
FEATURE [App::Link] D_2_D_SOD_123_611CB7E4_ln_060  label="D_41_2_D_SOD_123_611CBA7B"
  LinkPlacement = pos=(11.113,9.9695,-1.6) rot=(0.707107,0.707107,0;3.14159rad)
  LinkedObject = -> Shape004
  Placement = pos=(11.113,9.9695,-1.6) rot=(0.707107,0.707107,0;3.14159rad)
FEATURE [App::Link] D_2_D_SOD_123_611CB7E4_ln_061  label="D_40_2_D_SOD_123_611CBA6A"
  LinkPlacement = pos=(-7.937,9.9695,-1.6) rot=(0.707107,0.707107,0;3.14159rad)
  LinkedObject = -> Shape004
  Placement = pos=(-7.937,9.9695,-1.6) rot=(0.707107,0.707107,0;3.14159rad)
FEATURE [App::Link] D_2_D_SOD_123_611CB7E4_ln_062  label="D_39_2_D_SOD_123_611CBA59"
  LinkPlacement = pos=(-26.987,9.9695,-1.6) rot=(0.707107,0.707107,0;3.14159rad)
  LinkedObject = -> Shape004
  Placement = pos=(-26.987,9.9695,-1.6) rot=(0.707107,0.707107,0;3.14159rad)
FEATURE [App::Link] D_2_D_SOD_123_611CB7E4_ln_063  label="D_38_2_D_SOD_123_611CBA48"
  LinkPlacement = pos=(-61.976,9.9695,-1.6) rot=(0.707107,0.707107,0;3.14159rad)
  LinkedObject = -> Shape004
  Placement = pos=(-61.976,9.9695,-1.6) rot=(0.707107,0.707107,0;3.14159rad)
FEATURE [App::Link] D_2_D_SOD_123_611CB7E4_ln_064  label="D_37_2_D_SOD_123_611CBA37"
  LinkPlacement = pos=(-65.024,9.9695,-1.6) rot=(0.707107,0.707107,0;3.14159rad)
  LinkedObject = -> Shape004
  Placement = pos=(-65.024,9.9695,-1.6) rot=(0.707107,0.707107,0;3.14159rad)
FEATURE [App::Link] D_2_D_SOD_123_611CB7E4_ln_065  label="D_36_2_D_SOD_123_611CBA26"
  LinkPlacement = pos=(-84.1375,9.9695,-1.6) rot=(0.707107,0.707107,0;3.14159rad)
  LinkedObject = -> Shape004
  Placement = pos=(-84.1375,9.9695,-1.6) rot=(0.707107,0.707107,0;3.14159rad)
FEATURE [App::Link] D_2_D_SOD_123_611CB7E4_ln_066  label="D_35_2_D_SOD_123_611CBA15"
  LinkPlacement = pos=(-103.124,9.9695,-1.6) rot=(0.707107,0.707107,0;3.14159rad)
  LinkedObject = -> Shape004
  Placement = pos=(-103.124,9.9695,-1.6) rot=(0.707107,0.707107,0;3.14159rad)
FEATURE [App::Link] D_2_D_SOD_123_611CB7E4_ln_067  label="D_34_2_D_SOD_123_611CBA04"
  LinkPlacement = pos=(-122.047,9.9695,-1.6) rot=(0.707107,0.707107,0;3.14159rad)
  LinkedObject = -> Shape004
  Placement = pos=(-122.047,9.9695,-1.6) rot=(0.707107,0.707107,0;3.14159rad)
FEATURE [App::Link] D_2_D_SOD_123_611CB7E4_ln_068  label="D_33_2_D_SOD_123_611CB9F3"
  LinkPlacement = pos=(-141.224,3.4925,-1.6) rot=(0.707107,0.707107,0;3.14159rad)
  LinkedObject = -> Shape004
  Placement = pos=(-141.224,3.4925,-1.6) rot=(0.707107,0.707107,0;3.14159rad)
FEATURE [App::Link] D_2_D_SOD_123_611CB7E4_ln_069  label="D_32_2_D_SOD_123_611CB9E2"
  LinkPlacement = pos=(147.637,28.0035,-1.6) rot=(0.707107,0.707107,0;3.14159rad)
  LinkedObject = -> Shape004
  Placement = pos=(147.637,28.0035,-1.6) rot=(0.707107,0.707107,0;3.14159rad)
FEATURE [App::Link] D_2_D_SOD_123_611CB7E4_ln_070  label="D_31_2_D_SOD_123_611CB9D1"
  LinkPlacement = pos=(125.667,36.2585,-1.6) rot=(0.707107,0.707107,0;3.14159rad)
  LinkedObject = -> Shape004
  Placement = pos=(125.667,36.2585,-1.6) rot=(0.707107,0.707107,0;3.14159rad)
FEATURE [App::Link] D_2_D_SOD_123_611CB7E4_ln_071  label="D_30_2_D_SOD_123_611CB9C0"
  LinkPlacement = pos=(109.474,28.0035,-1.6) rot=(0.707107,0.707107,0;3.14159rad)
  LinkedObject = -> Shape004
  Placement = pos=(109.474,28.0035,-1.6) rot=(0.707107,0.707107,0;3.14159rad)
FEATURE [App::Link] D_2_D_SOD_123_611CB7E4_ln_072  label="D_29_2_D_SOD_123_611CB9AF"
  LinkPlacement = pos=(106.363,28.0035,-1.6) rot=(0.707107,0.707107,0;3.14159rad)
  LinkedObject = -> Shape004
  Placement = pos=(106.363,28.0035,-1.6) rot=(0.707107,0.707107,0;3.14159rad)
FEATURE [App::Link] D_2_D_SOD_123_611CB7E4_ln_073  label="D_28_2_D_SOD_123_611CB99E"
  LinkPlacement = pos=(87.313,28.0035,-1.6) rot=(0.707107,0.707107,0;3.14159rad)
  LinkedObject = -> Shape004
  Placement = pos=(87.313,28.0035,-1.6) rot=(0.707107,0.707107,0;3.14159rad)
FEATURE [App::Link] D_2_D_SOD_123_611CB7E4_ln_074  label="D_27_2_D_SOD_123_611CB98D"
  LinkPlacement = pos=(68.263,28.0035,-1.6) rot=(0.707107,0.707107,0;3.14159rad)
  LinkedObject = -> Shape004
  Placement = pos=(68.263,28.0035,-1.6) rot=(0.707107,0.707107,0;3.14159rad)
FEATURE [App::Link] D_2_D_SOD_123_611CB7E4_ln_075  label="D_26_2_D_SOD_123_611CB97C"
  LinkPlacement = pos=(49.213,28.0035,-1.6) rot=(0.707107,0.707107,0;3.14159rad)
  LinkedObject = -> Shape004
  Placement = pos=(49.213,28.0035,-1.6) rot=(0.707107,0.707107,0;3.14159rad)
FEATURE [App::Link] D_2_D_SOD_123_611CB7E4_ln_076  label="D_25_2_D_SOD_123_611CB96B"
  LinkPlacement = pos=(30.163,28.0035,-1.6) rot=(0.707107,0.707107,0;3.14159rad)
  LinkedObject = -> Shape004
  Placement = pos=(30.163,28.0035,-1.6) rot=(0.707107,0.707107,0;3.14159rad)
FEATURE [App::Link] D_2_D_SOD_123_611CB7E4_ln_077  label="D_24_2_D_SOD_123_611CB95A"
  LinkPlacement = pos=(11.113,28.0035,-1.6) rot=(0.707107,0.707107,0;3.14159rad)
  LinkedObject = -> Shape004
  Placement = pos=(11.113,28.0035,-1.6) rot=(0.707107,0.707107,0;3.14159rad)
FEATURE [App::Link] D_2_D_SOD_123_611CB7E4_ln_078  label="D_23_2_D_SOD_123_611CB949"
  LinkPlacement = pos=(-7.937,28.0035,-1.6) rot=(0.707107,0.707107,0;3.14159rad)
  LinkedObject = -> Shape004
  Placement = pos=(-7.937,28.0035,-1.6) rot=(0.707107,0.707107,0;3.14159rad)
FEATURE [App::Link] D_2_D_SOD_123_611CB7E4_ln_079  label="D_22_2_D_SOD_123_611CB938"
  LinkPlacement = pos=(-26.987,28.0035,-1.6) rot=(0.707107,0.707107,0;3.14159rad)
  LinkedObject = -> Shape004
  Placement = pos=(-26.987,28.0035,-1.6) rot=(0.707107,0.707107,0;3.14159rad)
FEATURE [App::Link] D_2_D_SOD_123_611CB7E4_ln_080  label="D_21_2_D_SOD_123_611CB927"
  LinkPlacement = pos=(-45.974,28.0035,-1.6) rot=(0.707107,0.707107,0;3.14159rad)
  LinkedObject = -> Shape004
  Placement = pos=(-45.974,28.0035,-1.6) rot=(0.707107,0.707107,0;3.14159rad)
FEATURE [App::Link] D_2_D_SOD_123_611CB7E4_ln_081  label="D_20_2_D_SOD_123_611CB916"
  LinkPlacement = pos=(-65.024,28.0035,-1.6) rot=(0.707107,0.707107,0;3.14159rad)
  LinkedObject = -> Shape004
  Placement = pos=(-65.024,28.0035,-1.6) rot=(0.707107,0.707107,0;3.14159rad)
FEATURE [App::Link] D_2_D_SOD_123_611CB7E4_ln_082  label="D_19_2_D_SOD_123_611CB905"
  LinkPlacement = pos=(-84.1375,28.0035,-1.6) rot=(0.707107,0.707107,0;3.14159rad)
  LinkedObject = -> Shape004
  Placement = pos=(-84.1375,28.0035,-1.6) rot=(0.707107,0.707107,0;3.14159rad)
FEATURE [App::Link] D_2_D_SOD_123_611CB7E4_ln_083  label="D_18_2_D_SOD_123_611CB8F4"
  LinkPlacement = pos=(-103.124,28.0035,-1.6) rot=(0.707107,0.707107,0;3.14159rad)
  LinkedObject = -> Shape004
  Placement = pos=(-103.124,28.0035,-1.6) rot=(0.707107,0.707107,0;3.14159rad)
FEATURE [App::Link] D_2_D_SOD_123_611CB7E4_ln_084  label="D_17_2_D_SOD_123_611CB8E3"
  LinkPlacement = pos=(-122.047,28.0035,-1.6) rot=(0.707107,0.707107,0;3.14159rad)
  LinkedObject = -> Shape004
  Placement = pos=(-122.047,28.0035,-1.6) rot=(0.707107,0.707107,0;3.14159rad)
FEATURE [App::Link] D_2_D_SOD_123_611CB7E4_ln_085  label="D_16_2_D_SOD_123_611CB8D2"
  LinkPlacement = pos=(128.587,47.371,-1.6) rot=(0.707107,0.707107,0;3.14159rad)
  LinkedObject = -> Shape004
  Placement = pos=(128.587,47.371,-1.6) rot=(0.707107,0.707107,0;3.14159rad)
FEATURE [App::Link] D_2_D_SOD_123_611CB7E4_ln_086  label="D_15_2_D_SOD_123_611CB8C1"
  LinkPlacement = pos=(125.667,47.371,-1.6) rot=(0.707107,0.707107,0;3.14159rad)
  LinkedObject = -> Shape004
  Placement = pos=(125.667,47.371,-1.6) rot=(0.707107,0.707107,0;3.14159rad)
FEATURE [App::Link] D_2_D_SOD_123_611CB7E4_ln_087  label="D_14_2_D_SOD_123_611CB8B0"
  LinkPlacement = pos=(106.363,47.371,-1.6) rot=(0.707107,0.707107,0;3.14159rad)
  LinkedObject = -> Shape004
  Placement = pos=(106.363,47.371,-1.6) rot=(0.707107,0.707107,0;3.14159rad)
FEATURE [App::Link] D_2_D_SOD_123_611CB7E4_ln_088  label="D_13_2_D_SOD_123_611CB89F"
  LinkPlacement = pos=(87.313,47.371,-1.6) rot=(0.707107,0.707107,0;3.14159rad)
  LinkedObject = -> Shape004
  Placement = pos=(87.313,47.371,-1.6) rot=(0.707107,0.707107,0;3.14159rad)
FEATURE [App::Link] D_2_D_SOD_123_611CB7E4_ln_089  label="D_12_2_D_SOD_123_611CB88E"
  LinkPlacement = pos=(68.263,47.371,-1.6) rot=(0.707107,0.707107,0;3.14159rad)
  LinkedObject = -> Shape004
  Placement = pos=(68.263,47.371,-1.6) rot=(0.707107,0.707107,0;3.14159rad)
FEATURE [App::Link] D_2_D_SOD_123_611CB7E4_ln_090  label="D_11_2_D_SOD_123_611CB87D"
  LinkPlacement = pos=(49.213,47.371,-1.6) rot=(0.707107,0.707107,0;3.14159rad)
  LinkedObject = -> Shape004
  Placement = pos=(49.213,47.371,-1.6) rot=(0.707107,0.707107,0;3.14159rad)
FEATURE [App::Link] D_2_D_SOD_123_611CB7E4_ln_091  label="D_10_2_D_SOD_123_611CB86C"
  LinkPlacement = pos=(30.163,47.371,-1.6) rot=(0.707107,0.707107,0;3.14159rad)
  LinkedObject = -> Shape004
  Placement = pos=(30.163,47.371,-1.6) rot=(0.707107,0.707107,0;3.14159rad)
FEATURE [App::Link] D_2_D_SOD_123_611CB7E4_ln_092  label="D_9_2_D_SOD_123_611CB85B"
  LinkPlacement = pos=(11.113,47.371,-1.6) rot=(0.707107,0.707107,0;3.14159rad)
  LinkedObject = -> Shape004
  Placement = pos=(11.113,47.371,-1.6) rot=(0.707107,0.707107,0;3.14159rad)
FEATURE [App::Link] D_2_D_SOD_123_611CB7E4_ln_093  label="D_8_2_D_SOD_123_611CB84A"
  LinkPlacement = pos=(-7.937,47.371,-1.6) rot=(0.707107,0.707107,0;3.14159rad)
  LinkedObject = -> Shape004
  Placement = pos=(-7.937,47.371,-1.6) rot=(0.707107,0.707107,0;3.14159rad)
FEATURE [App::Link] D_2_D_SOD_123_611CB7E4_ln_094  label="D_7_2_D_SOD_123_611CB839"
  LinkPlacement = pos=(-26.987,47.371,-1.6) rot=(0.707107,0.707107,0;3.14159rad)
  LinkedObject = -> Shape004
  Placement = pos=(-26.987,47.371,-1.6) rot=(0.707107,0.707107,0;3.14159rad)
FEATURE [App::Link] D_2_D_SOD_123_611CB7E4_ln_095  label="D_6_2_D_SOD_123_611CB828"
  LinkPlacement = pos=(-45.974,47.371,-1.6) rot=(0.707107,0.707107,0;3.14159rad)
  LinkedObject = -> Shape004
  Placement = pos=(-45.974,47.371,-1.6) rot=(0.707107,0.707107,0;3.14159rad)
FEATURE [App::Link] D_2_D_SOD_123_611CB7E4_ln_096  label="D_5_2_D_SOD_123_611CB817"
  LinkPlacement = pos=(-65.024,47.371,-1.6) rot=(0.707107,0.707107,0;3.14159rad)
  LinkedObject = -> Shape004
  Placement = pos=(-65.024,47.371,-1.6) rot=(0.707107,0.707107,0;3.14159rad)
FEATURE [App::Link] D_2_D_SOD_123_611CB7E4_ln_097  label="D_4_2_D_SOD_123_611CB806"
  LinkPlacement = pos=(-84.1375,47.371,-1.6) rot=(0.707107,0.707107,0;3.14159rad)
  LinkedObject = -> Shape004
  Placement = pos=(-84.1375,47.371,-1.6) rot=(0.707107,0.707107,0;3.14159rad)
FEATURE [App::Link] D_2_D_SOD_123_611CB7E4_ln_098  label="D_3_2_D_SOD_123_611CB7F5"
  LinkPlacement = pos=(-103.124,47.371,-1.6) rot=(0.707107,0.707107,0;3.14159rad)
  LinkedObject = -> Shape004
  Placement = pos=(-103.124,47.371,-1.6) rot=(0.707107,0.707107,0;3.14159rad)
FEATURE [App::Link] D_2_D_SOD_123_611CB7E4_ln_099  label="D26_2_D_SOD_123_611CB7C2"
  LinkPlacement = pos=(-141.224,22.2885,-1.6) rot=(0.707107,0.707107,0;3.14159rad)
  LinkedObject = -> Shape004
  Placement = pos=(-141.224,22.2885,-1.6) rot=(0.707107,0.707107,0;3.14159rad)
FEATURE [Part::Feature] Shape005  label="D3_LED_WS2812B_PLCC4_50x50mm_P32mm_611CB5AF"
  Placement = pos=(3.048,19.05,-1.6) rot=(0,1,0;3.14159rad)
  shape: bbox 5.4 x 5 x 1.6 mm, 68 faces (baked)
FEATURE [Part::Feature] Part__Feature007  label="SOLID001"
  shape: bbox 13.86 x 30.2 x 14.85 mm, 421 faces (baked)
FEATURE [Part::Feature] Part__Feature008  label="COMPOUND"
  shape: bbox 8.6 x 30.2 x 10 mm, 0 faces, 0 solids (baked)
FEATURE [App::Part] PEC11R_4220K_L13_8_W12_4_H26_5  label="K_1_PEC11R-4220K_L13-8_W12-4_H26-5_611CBEC7"
  Group = -> [Part__Feature007,Part__Feature008]
  Origin = -> Origin010
  Placement = pos=(136.525,47.625,0) rot=(1,0,0;1.5708rad)
FEATURE [Part::Feature] Shape006  label="K_1_Rotary knob v4_611CBEC7[2]"
  Placement = pos=(136.525,47.625,10) rot=(1,0,0;1.5708rad)
  shape: bbox 12 x 12 x 18 mm, 33 faces (baked)
FEATURE [App::Part] Top_e1db
  Group = -> [Shape,Shape001,K_105_cherry_mx_611CBFA4_ln_,K_105_MX______________________________________1_______611CBFA4_2__ln_,K_105_cherry_mx_611CBFA4_ln_001,K_105_MX______________________________________1_______611CBFA4_2__ln_001,K_105_cherry_mx_611CBFA4_ln_002,K_105_MX______________________________________1_______611CBFA4_2__ln_002,K_105_cherry_mx_611CBFA4_ln_003,+205 more]
  Origin = -> Origin003
FEATURE [Part::Feature] Shape007  label="J1_(Unsaved)_611F973D"
  Placement = pos=(-165.556,28.575,-1.6) rot=(0.707107,0.707107,0;3.14159rad)
  shape: bbox 7.903 x 8.943 x 4.203 mm, 384 faces, 24 solids (baked)
FEATURE [Part::Feature] Shape008  label="Y1_Crystal_SMD_3225-4Pin_3.2x2.5mm_611CC0DE"
  Placement = pos=(-33.972,0.8255,-1.6) rot=(0.92388,0.382683,0;3.14159rad)
  shape: bbox 3.891 x 3.889 x 0.64 mm, 28 faces (baked)
FEATURE [Part::Feature] Shape009  label="U3_LQFP_64_10x10mm_P05mm_611CC0CC"
  Placement = pos=(-44.704,1.5875,-1.6) rot=(0,1,0;3.14159rad)
  shape: bbox 12 x 12 x 1.5 mm, 1004 faces (baked)
FEATURE [Part::Feature] Shape010  label="U2_SOT_23_6_611CC061"
  Placement = pos=(-157.162,28.575,-1.6) rot=(1,0,0;3.14159rad)
  shape: bbox 2.8 x 2.9 x 1.55 mm, 124 faces (baked)
FEATURE [Part::Feature] Shape011  label="U1_SOT_23_5_611CC04B"
  Placement = pos=(-82.55,19.05,-1.6) rot=(1,0,0;3.14159rad)
  shape: bbox 2.8 x 2.9 x 1.55 mm, 109 faces (baked)
FEATURE [Part::Feature] Shape012  label="SW1_EVQPUC02K_611CC036"
  Placement = pos=(-158.75,42.8625,-1.6) rot=(0.57735,0.57735,-0.57735;4.18879rad)
  shape: bbox 4.542 x 6.402 x 2.183 mm, 274 faces (baked)
FEATURE [App::Link] R7_R_0603_1608Metric_611CC01B_ln_011  label="R5_R_0603_1608Metric_611CC007"
  LinkPlacement = pos=(-53.848,3.2385,-1.6) rot=(0,1,0;3.14159rad)
  LinkedObject = -> Shape002
  Placement = pos=(-53.848,3.2385,-1.6) rot=(0,1,0;3.14159rad)
FEATURE [Part::Feature] Shape013  label="Q2_SOT_23_611CBFCE"
  Placement = pos=(-143.256,27.305,-1.6) rot=(0.707107,0.707107,0;3.14159rad)
  shape: bbox 3 x 2.5 x 1.2 mm, 76 faces (baked)
FEATURE [App::Link] Q2_SOT_23_611CBFCE_ln_  label="Q1_SOT_23_611CBFB9"
  LinkPlacement = pos=(-98.425,38.1,-1.6) rot=(0,1,0;3.14159rad)
  LinkedObject = -> Shape013
  Placement = pos=(-98.425,38.1,-1.6) rot=(0,1,0;3.14159rad)
FEATURE [Part::Feature] Shape014  label="J2_PinHeader_1x06_P254mm_Vertical_611CBEB1"
  Placement = pos=(-147.828,33.9725,-1.6) rot=(0,1,0;3.14159rad)
  shape: bbox 2.54 x 15.24 x 11.54 mm, 148 faces (baked)
FEATURE [Part::Feature] Shape015  label="F1_User Library-ptc06032-1_611CBE77"
  Placement = pos=(-151.939,32.8295,-1.6) rot=(0,1,0;3.14159rad)
  shape: bbox 1.6 x 0.75 x 0.755 mm, 42 faces (baked)
FEATURE [App::Link] D3_LED_WS2812B_PLCC4_50x50mm_P32mm_611CB5AF_ln_  label="D20_LED_WS2812B_PLCC4_50x50mm_P32mm_611CB736"
  LinkPlacement = pos=(-120.65,-38.0995,-1.6) rot=(0,1,0;3.14159rad)
  LinkedObject = -> Shape005
  Placement = pos=(-120.65,-38.0995,-1.6) rot=(0,1,0;3.14159rad)
FEATURE [App::Link] D3_LED_WS2812B_PLCC4_50x50mm_P32mm_611CB5AF_ln_001  label="D19_LED_WS2812B_PLCC4_50x50mm_P32mm_611CB71F"
  LinkPlacement = pos=(-63.627,-38.0995,-1.6) rot=(0,1,0;3.14159rad)
  LinkedObject = -> Shape005
  Placement = pos=(-63.627,-38.0995,-1.6) rot=(0,1,0;3.14159rad)
FEATURE [App::Link] D3_LED_WS2812B_PLCC4_50x50mm_P32mm_611CB5AF_ln_002  label="D18_LED_WS2812B_PLCC4_50x50mm_P32mm_611CB708"
  LinkPlacement = pos=(3.048,-38.0995,-1.6) rot=(0,1,0;3.14159rad)
  LinkedObject = -> Shape005
  Placement = pos=(3.048,-38.0995,-1.6) rot=(0,1,0;3.14159rad)
FEATURE [App::Link] D3_LED_WS2812B_PLCC4_50x50mm_P32mm_611CB5AF_ln_003  label="D17_LED_WS2812B_PLCC4_50x50mm_P32mm_611CB6F1"
  LinkPlacement = pos=(69.799,-38.0995,-1.6) rot=(0,1,0;3.14159rad)
  LinkedObject = -> Shape005
  Placement = pos=(69.799,-38.0995,-1.6) rot=(0,1,0;3.14159rad)
FEATURE [App::Link] D3_LED_WS2812B_PLCC4_50x50mm_P32mm_611CB5AF_ln_004  label="D16_LED_WS2812B_PLCC4_50x50mm_P32mm_611CB6DA"
  LinkPlacement = pos=(127,-38.0995,-1.6) rot=(0,1,0;3.14159rad)
  LinkedObject = -> Shape005
  Placement = pos=(127,-38.0995,-1.6) rot=(0,1,0;3.14159rad)
FEATURE [App::Link] D3_LED_WS2812B_PLCC4_50x50mm_P32mm_611CB5AF_ln_005  label="D15_LED_WS2812B_PLCC4_50x50mm_P32mm_611CB6C3"
  LinkPlacement = pos=(127,-19.0495,-1.6) rot=(0,1,0;3.14159rad)
  LinkedObject = -> Shape005
  Placement = pos=(127,-19.0495,-1.6) rot=(0,1,0;3.14159rad)
FEATURE [App::Link] D3_LED_WS2812B_PLCC4_50x50mm_P32mm_611CB5AF_ln_006  label="D14_LED_WS2812B_PLCC4_50x50mm_P32mm_611CB6AC"
  LinkPlacement = pos=(69.799,-19.0495,-1.6) rot=(0,1,0;3.14159rad)
  LinkedObject = -> Shape005
  Placement = pos=(69.799,-19.0495,-1.6) rot=(0,1,0;3.14159rad)
FEATURE [App::Link] D3_LED_WS2812B_PLCC4_50x50mm_P32mm_611CB5AF_ln_007  label="D13_LED_WS2812B_PLCC4_50x50mm_P32mm_611CB695"
  LinkPlacement = pos=(3.048,-19.0495,-1.6) rot=(0,1,0;3.14159rad)
  LinkedObject = -> Shape005
  Placement = pos=(3.048,-19.0495,-1.6) rot=(0,1,0;3.14159rad)
FEATURE [App::Link] D3_LED_WS2812B_PLCC4_50x50mm_P32mm_611CB5AF_ln_008  label="D12_LED_WS2812B_PLCC4_50x50mm_P32mm_611CB67E"
  LinkPlacement = pos=(-63.627,-19.0495,-1.6) rot=(0,1,0;3.14159rad)
  LinkedObject = -> Shape005
  Placement = pos=(-63.627,-19.0495,-1.6) rot=(0,1,0;3.14159rad)
FEATURE [App::Link] D3_LED_WS2812B_PLCC4_50x50mm_P32mm_611CB5AF_ln_009  label="D11_LED_WS2812B_PLCC4_50x50mm_P32mm_611CB667"
  LinkPlacement = pos=(-120.65,-19.0495,-1.6) rot=(0,1,0;3.14159rad)
  LinkedObject = -> Shape005
  Placement = pos=(-120.65,-19.0495,-1.6) rot=(0,1,0;3.14159rad)
FEATURE [App::Link] D3_LED_WS2812B_PLCC4_50x50mm_P32mm_611CB5AF_ln_010  label="D10_LED_WS2812B_PLCC4_50x50mm_P32mm_611CB650"
  LinkPlacement = pos=(-120.65,0,-1.6) rot=(0,1,0;3.14159rad)
  LinkedObject = -> Shape005
  Placement = pos=(-120.65,0,-1.6) rot=(0,1,0;3.14159rad)
FEATURE [App::Link] D3_LED_WS2812B_PLCC4_50x50mm_P32mm_611CB5AF_ln_011  label="D9_LED_WS2812B_PLCC4_50x50mm_P32mm_611CB639"
  LinkPlacement = pos=(-63.627,0,-1.6) rot=(0,1,0;3.14159rad)
  LinkedObject = -> Shape005
  Placement = pos=(-63.627,0,-1.6) rot=(0,1,0;3.14159rad)
FEATURE [App::Link] D3_LED_WS2812B_PLCC4_50x50mm_P32mm_611CB5AF_ln_012  label="D8_LED_WS2812B_PLCC4_50x50mm_P32mm_611CB622"
  LinkPlacement = pos=(3.048,0,-1.6) rot=(0,1,0;3.14159rad)
  LinkedObject = -> Shape005
  Placement = pos=(3.048,0,-1.6) rot=(0,1,0;3.14159rad)
FEATURE [App::Link] D3_LED_WS2812B_PLCC4_50x50mm_P32mm_611CB5AF_ln_013  label="D7_LED_WS2812B_PLCC4_50x50mm_P32mm_611CB60B"
  LinkPlacement = pos=(69.799,0,-1.6) rot=(0,1,0;3.14159rad)
  LinkedObject = -> Shape005
  Placement = pos=(69.799,0,-1.6) rot=(0,1,0;3.14159rad)
FEATURE [App::Link] D3_LED_WS2812B_PLCC4_50x50mm_P32mm_611CB5AF_ln_014  label="D6_LED_WS2812B_PLCC4_50x50mm_P32mm_611CB5F4"
  LinkPlacement = pos=(127,0,-1.6) rot=(0,1,0;3.14159rad)
  LinkedObject = -> Shape005
  Placement = pos=(127,0,-1.6) rot=(0,1,0;3.14159rad)
FEATURE [App::Link] D3_LED_WS2812B_PLCC4_50x50mm_P32mm_611CB5AF_ln_015  label="D5_LED_WS2812B_PLCC4_50x50mm_P32mm_611CB5DD"
  LinkPlacement = pos=(127,19.05,-1.6) rot=(0,1,0;3.14159rad)
  LinkedObject = -> Shape005
  Placement = pos=(127,19.05,-1.6) rot=(0,1,0;3.14159rad)
FEATURE [App::Link] D3_LED_WS2812B_PLCC4_50x50mm_P32mm_611CB5AF_ln_016  label="D4_LED_WS2812B_PLCC4_50x50mm_P32mm_611CB5C6"
  LinkPlacement = pos=(69.799,19.05,-1.6) rot=(0,1,0;3.14159rad)
  LinkedObject = -> Shape005
  Placement = pos=(69.799,19.05,-1.6) rot=(0,1,0;3.14159rad)
FEATURE [App::Link] D3_LED_WS2812B_PLCC4_50x50mm_P32mm_611CB5AF_ln_017  label="D2_LED_WS2812B_PLCC4_50x50mm_P32mm_611E9F10"
  LinkPlacement = pos=(-63.627,19.05,-1.6) rot=(0,1,0;3.14159rad)
  LinkedObject = -> Shape005
  Placement = pos=(-63.627,19.05,-1.6) rot=(0,1,0;3.14159rad)
FEATURE [App::Link] D3_LED_WS2812B_PLCC4_50x50mm_P32mm_611CB5AF_ln_018  label="D1_LED_WS2812B_PLCC4_50x50mm_P32mm_611CB581"
  LinkPlacement = pos=(-120.65,19.05,-1.6) rot=(0,1,0;3.14159rad)
  LinkedObject = -> Shape005
  Placement = pos=(-120.65,19.05,-1.6) rot=(0,1,0;3.14159rad)
FEATURE [Part::Feature] Shape016  label="BZ1_Buzzer_Murata_PKMCS0909E4000_R1_611CB3F8"
  Placement = pos=(-20.066,0.0635,-1.6) rot=(1,0,0;3.14159rad)
  shape: bbox 9 x 9 x 1.9 mm, 41 faces (baked)
FEATURE [App::Part] Bot_e1db
  Group = -> [Shape002,R7_R_0603_1608Metric_611CC01B_ln_,R7_R_0603_1608Metric_611CC01B_ln_001,R7_R_0603_1608Metric_611CC01B_ln_002,R7_R_0603_1608Metric_611CC01B_ln_003,R7_R_0603_1608Metric_611CC01B_ln_004,R7_R_0603_1608Metric_611CC01B_ln_005,R7_R_0603_1608Metric_611CC01B_ln_006,R7_R_0603_1608Metric_611CC01B_ln_007,R7_R_0603_1608Metric_611CC01B_ln_008,R7_R_0603_1608Metric_611CC01B_ln_009,+171 more]
  Origin = -> Origin004
FEATURE [App::Part] Step_Models_e1db
  Group = -> [Top_e1db,Bot_e1db]
  Origin = -> Origin002
FEATURE [Part::Feature] botSilks_1a36
  Placement = pos=(-174.625,80.9625,-1.67) rot=(0,0,1;0rad)
  shape: large baked B-rep (64 MB .brp); summary skipped
FEATURE [Part::Feature] topSilks_dbf0
  Placement = pos=(-174.625,80.9625,0.07) rot=(0,0,1;0rad)
  shape: large baked B-rep (258 MB .brp); summary skipped
FEATURE [Part::Feature] topTracks_e1db
  Placement = pos=(-174.625,80.9625,0.01) rot=(0,0,1;0rad)
  shape: bbox 335.5 x 119.6 x 0.04 mm, 420 faces, 0 solids (baked)
FEATURE [Part::Feature] botTracks_e1db
  Placement = pos=(-174.625,80.9625,-1.61) rot=(0,0,1;0rad)
  shape: bbox 335.5 x 119.6 x 0.04 mm, 1357 faces, 0 solids (baked)
FEATURE [App::Part] Board_Geoms_e1db
  Group = -> [Local_CS_e1db,Pcb_e1db,PCB_Sketch_e1db,botSilks_1a36,topSilks_dbf0,topTracks_e1db,botTracks_e1db]
  Origin = -> Origin
FEATURE [App::Part] Board_e1db  label="Orthonite87_PCB"
  Group = -> [Board_Geoms_e1db,Step_Models_e1db]
  Origin = -> Origin001
